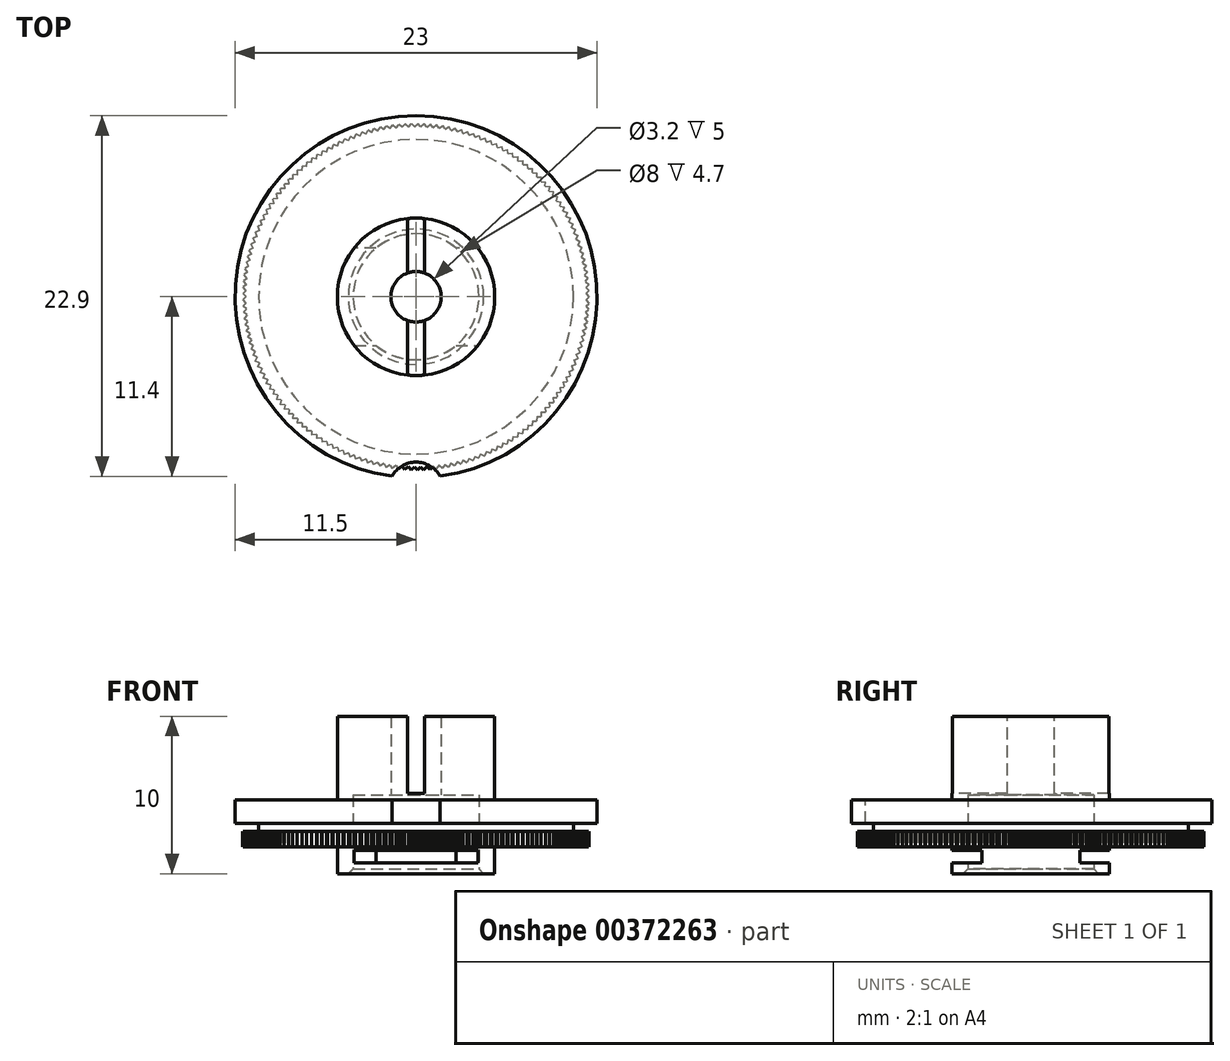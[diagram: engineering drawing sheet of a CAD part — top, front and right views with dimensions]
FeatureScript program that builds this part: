
annotation { "Feature Type Name" : "Feature", "Feature Type Description" : "" }
export const myFeature = defineFeature(function(context is Context, id is Id, definition is map)
    precondition{}
    {
        {
            var Q0;
            Q0=qCreatedBy(makeId("Front.planeOp"),FACE);
            var sketch = newSketch(context, id + "F0", { "sketchPlane" : qUnion([Q0])});
            skLineSegment(sketch, "E0", {"start": v(5, 0) * mm, "end": v(5, 1.7) * mm});
            skLineSegment(sketch, "E1", {"start": v(5, 1.7) * mm, "end": v(11, 1.7) * mm});
            skLineSegment(sketch, "E2", {"start": v(11, 1.7) * mm, "end": v(11, 2.7) * mm});
            skLineSegment(sketch, "E3", {"start": v(11, 2.7) * mm, "end": v(10, 2.7) * mm});
            skLineSegment(sketch, "E4", {"start": v(10, 2.7) * mm, "end": v(10, 3.2) * mm});
            skLineSegment(sketch, "E5", {"start": v(10, 3.2) * mm, "end": v(11.5, 3.2) * mm});
            skLineSegment(sketch, "E6", {"start": v(11.5, 3.2) * mm, "end": v(11.5, 4.7) * mm});
            skLineSegment(sketch, "E7", {"start": v(11.5, 4.7) * mm, "end": v(5, 4.7) * mm});
            skLineSegment(sketch, "E8", {"start": v(5, 4.7) * mm, "end": v(5, 10) * mm});
            skLineSegment(sketch, "E9", {"start": v(5, 10) * mm, "end": v(1.6, 10) * mm});
            skLineSegment(sketch, "E10", {"start": v(1.6, 10) * mm, "end": v(1.6, 5) * mm});
            skLineSegment(sketch, "E11", {"start": v(1.6, 5) * mm, "end": v(4, 5) * mm});
            skLineSegment(sketch, "E12", {"start": v(4, 5) * mm, "end": v(4, 0.3) * mm});
            skLineSegment(sketch, "E13", {"start": v(4, 0.3) * mm, "end": v(4.3, 0) * mm});
            skLineSegment(sketch, "E14", {"start": v(4.3, 0) * mm, "end": v(5, 0) * mm});
            skLineSegment(sketch, "E15", {"start": v(0, 0) * mm, "end": v(0, 10) * mm, "construction": true});
            skSolve(sketch);
        }
        {
            var Q0;
            Q0=makeQuery(id+"F0.imprint","IMPRINT",FACE,{"disambiguationData":[TD([[makeQuery(id+"F0.imprint","IMPRINT",EDGE,{"derivedFrom":sQuery(id+"F0.wireOp",EDGE,"E0")}),1.0]])]});
            var Q1;
            Q1=sQuery(id+"F0.wireOp",EDGE,"E15");
            revolve(context, id + "F1", {"entities" : qUnion([Q0]), "axis" : qUnion([Q1]), "revolveType" : RevolveType.FULL});
        }
        {
            var Q0;
            Q0=makeQuery(id+"F1.opRevolve","SWEPT_FACE",FACE,{"disambiguationData":[OSD([sQuery(id+"F0.wireOp",EDGE,"E1")])]});
            var sketch = newSketch(context, id + "F2", { "sketchPlane" : qUnion([Q0])});
            skCircle(sketch, "E16", {"center": v(0, 0) * mm, "radius": 10.8 * mm});
            skLineSegment(sketch, "E17", {"start": v(-10.8, 0) * mm, "end": v(-11, 0.18) * mm});
            skLineSegment(sketch, "E18", {"start": v(-10.8, 0) * mm, "end": v(-11, -0.22) * mm});
            skLineSegment(sketch, "E19", {"start": v(-10.8, 0) * mm, "end": v(-11, 0) * mm, "construction": true});
            skSolve(sketch);
        }
        {
            var Q0;
            {var subQ2=sQuery(id+"F2.wireOp",EDGE,"E17");Q0=makeQuery(id+"F2.imprint","IMPRINT",FACE,{"disambiguationData":[TD([[makeQuery(id+"F2.imprint","IMPRINT",EDGE,{"derivedFrom":subQ2}),1.0]])]});}
            var Q1;
            Q1=makeQuery(id+"F1.opRevolve","SWEPT_FACE",FACE,{"disambiguationData":[OSD([sQuery(id+"F0.wireOp",EDGE,"E3")])]});
            extrude(context, id + "F3", {"entities" : qUnion([Q0]), "endBound" : BoundingType.UP_TO_SURFACE, "oppositeDirection" : true, "endBoundEntityFace" : qUnion([Q1]), "depth" : 25 * mm});
        }
        {
            var Q0;
            Q0=makeQuery(id+"F3.opExtrude","SWEPT_BODY",BODY,{"disambiguationData":[OSD([sQuery(id+"F0.wireOp",EDGE,"E1"),sQuery(id+"F0.wireOp",EDGE,"E2"),sQuery(id+"F2.wireOp",EDGE,"E17"),sQuery(id+"F2.wireOp",EDGE,"E18")])]});
            var Q1;
            Q1=sQuery(id+"F0.wireOp",EDGE,"E15");
            circularPattern(context, id + "F4", {"entities" : qUnion([Q0]), "axis" : qUnion([Q1]), "angle" : 357.93 * degree, "instanceCount" : round(173), "equalSpace" : true, "computeTransformsWithoutBuiltin" : true});
        }
        {
            var Q0;
            Q0=makeQuery(id+"F4.opPattern","COPY",BODY,{"derivedFrom":makeQuery(id+"F3.opExtrude","SWEPT_BODY",BODY,{"disambiguationData":[OSD([sQuery(id+"F0.wireOp",EDGE,"E1"),sQuery(id+"F0.wireOp",EDGE,"E2"),sQuery(id+"F2.wireOp",EDGE,"E17"),sQuery(id+"F2.wireOp",EDGE,"E18")])]}),"instanceName":"168"});
            var Q1;
            Q1=makeQuery(id+"F4.opPattern","COPY",BODY,{"derivedFrom":makeQuery(id+"F3.opExtrude","SWEPT_BODY",BODY,{"disambiguationData":[OSD([sQuery(id+"F0.wireOp",EDGE,"E1"),sQuery(id+"F0.wireOp",EDGE,"E2"),sQuery(id+"F2.wireOp",EDGE,"E17"),sQuery(id+"F2.wireOp",EDGE,"E18")])]}),"instanceName":"7"});
            var Q2;
            Q2=makeQuery(id+"F4.opPattern","COPY",BODY,{"derivedFrom":makeQuery(id+"F3.opExtrude","SWEPT_BODY",BODY,{"disambiguationData":[OSD([sQuery(id+"F0.wireOp",EDGE,"E1"),sQuery(id+"F0.wireOp",EDGE,"E2"),sQuery(id+"F2.wireOp",EDGE,"E17"),sQuery(id+"F2.wireOp",EDGE,"E18")])]}),"instanceName":"55"});
            var Q3;
            Q3=makeQuery(id+"F4.opPattern","COPY",BODY,{"derivedFrom":makeQuery(id+"F3.opExtrude","SWEPT_BODY",BODY,{"disambiguationData":[OSD([sQuery(id+"F0.wireOp",EDGE,"E1"),sQuery(id+"F0.wireOp",EDGE,"E2"),sQuery(id+"F2.wireOp",EDGE,"E17"),sQuery(id+"F2.wireOp",EDGE,"E18")])]}),"instanceName":"157"});
            var Q4;
            Q4=makeQuery(id+"F4.opPattern","COPY",BODY,{"derivedFrom":makeQuery(id+"F3.opExtrude","SWEPT_BODY",BODY,{"disambiguationData":[OSD([sQuery(id+"F0.wireOp",EDGE,"E1"),sQuery(id+"F0.wireOp",EDGE,"E2"),sQuery(id+"F2.wireOp",EDGE,"E17"),sQuery(id+"F2.wireOp",EDGE,"E18")])]}),"instanceName":"36"});
            var Q5;
            Q5=makeQuery(id+"F4.opPattern","COPY",BODY,{"derivedFrom":makeQuery(id+"F3.opExtrude","SWEPT_BODY",BODY,{"disambiguationData":[OSD([sQuery(id+"F0.wireOp",EDGE,"E1"),sQuery(id+"F0.wireOp",EDGE,"E2"),sQuery(id+"F2.wireOp",EDGE,"E17"),sQuery(id+"F2.wireOp",EDGE,"E18")])]}),"instanceName":"127"});
            var Q6;
            Q6=makeQuery(id+"F4.opPattern","COPY",BODY,{"derivedFrom":makeQuery(id+"F3.opExtrude","SWEPT_BODY",BODY,{"disambiguationData":[OSD([sQuery(id+"F0.wireOp",EDGE,"E1"),sQuery(id+"F0.wireOp",EDGE,"E2"),sQuery(id+"F2.wireOp",EDGE,"E17"),sQuery(id+"F2.wireOp",EDGE,"E18")])]}),"instanceName":"138"});
            var Q7;
            Q7=makeQuery(id+"F4.opPattern","COPY",BODY,{"derivedFrom":makeQuery(id+"F3.opExtrude","SWEPT_BODY",BODY,{"disambiguationData":[OSD([sQuery(id+"F0.wireOp",EDGE,"E1"),sQuery(id+"F0.wireOp",EDGE,"E2"),sQuery(id+"F2.wireOp",EDGE,"E17"),sQuery(id+"F2.wireOp",EDGE,"E18")])]}),"instanceName":"3"});
            var Q8;
            Q8=makeQuery(id+"F4.opPattern","COPY",BODY,{"derivedFrom":makeQuery(id+"F3.opExtrude","SWEPT_BODY",BODY,{"disambiguationData":[OSD([sQuery(id+"F0.wireOp",EDGE,"E1"),sQuery(id+"F0.wireOp",EDGE,"E2"),sQuery(id+"F2.wireOp",EDGE,"E17"),sQuery(id+"F2.wireOp",EDGE,"E18")])]}),"instanceName":"66"});
            var Q9;
            Q9=makeQuery(id+"F4.opPattern","COPY",BODY,{"derivedFrom":makeQuery(id+"F3.opExtrude","SWEPT_BODY",BODY,{"disambiguationData":[OSD([sQuery(id+"F0.wireOp",EDGE,"E1"),sQuery(id+"F0.wireOp",EDGE,"E2"),sQuery(id+"F2.wireOp",EDGE,"E17"),sQuery(id+"F2.wireOp",EDGE,"E18")])]}),"instanceName":"4"});
            var Q10;
            Q10=makeQuery(id+"F4.opPattern","COPY",BODY,{"derivedFrom":makeQuery(id+"F3.opExtrude","SWEPT_BODY",BODY,{"disambiguationData":[OSD([sQuery(id+"F0.wireOp",EDGE,"E1"),sQuery(id+"F0.wireOp",EDGE,"E2"),sQuery(id+"F2.wireOp",EDGE,"E17"),sQuery(id+"F2.wireOp",EDGE,"E18")])]}),"instanceName":"39"});
            var Q11;
            Q11=makeQuery(id+"F4.opPattern","COPY",BODY,{"derivedFrom":makeQuery(id+"F3.opExtrude","SWEPT_BODY",BODY,{"disambiguationData":[OSD([sQuery(id+"F0.wireOp",EDGE,"E1"),sQuery(id+"F0.wireOp",EDGE,"E2"),sQuery(id+"F2.wireOp",EDGE,"E17"),sQuery(id+"F2.wireOp",EDGE,"E18")])]}),"instanceName":"67"});
            var Q12;
            Q12=makeQuery(id+"F4.opPattern","COPY",BODY,{"derivedFrom":makeQuery(id+"F3.opExtrude","SWEPT_BODY",BODY,{"disambiguationData":[OSD([sQuery(id+"F0.wireOp",EDGE,"E1"),sQuery(id+"F0.wireOp",EDGE,"E2"),sQuery(id+"F2.wireOp",EDGE,"E17"),sQuery(id+"F2.wireOp",EDGE,"E18")])]}),"instanceName":"65"});
            var Q13;
            Q13=makeQuery(id+"F4.opPattern","COPY",BODY,{"derivedFrom":makeQuery(id+"F3.opExtrude","SWEPT_BODY",BODY,{"disambiguationData":[OSD([sQuery(id+"F0.wireOp",EDGE,"E1"),sQuery(id+"F0.wireOp",EDGE,"E2"),sQuery(id+"F2.wireOp",EDGE,"E17"),sQuery(id+"F2.wireOp",EDGE,"E18")])]}),"instanceName":"41"});
            var Q14;
            Q14=makeQuery(id+"F4.opPattern","COPY",BODY,{"derivedFrom":makeQuery(id+"F3.opExtrude","SWEPT_BODY",BODY,{"disambiguationData":[OSD([sQuery(id+"F0.wireOp",EDGE,"E1"),sQuery(id+"F0.wireOp",EDGE,"E2"),sQuery(id+"F2.wireOp",EDGE,"E17"),sQuery(id+"F2.wireOp",EDGE,"E18")])]}),"instanceName":"82"});
            var Q15;
            Q15=makeQuery(id+"F4.opPattern","COPY",BODY,{"derivedFrom":makeQuery(id+"F3.opExtrude","SWEPT_BODY",BODY,{"disambiguationData":[OSD([sQuery(id+"F0.wireOp",EDGE,"E1"),sQuery(id+"F0.wireOp",EDGE,"E2"),sQuery(id+"F2.wireOp",EDGE,"E17"),sQuery(id+"F2.wireOp",EDGE,"E18")])]}),"instanceName":"45"});
            var Q16;
            Q16=makeQuery(id+"F4.opPattern","COPY",BODY,{"derivedFrom":makeQuery(id+"F3.opExtrude","SWEPT_BODY",BODY,{"disambiguationData":[OSD([sQuery(id+"F0.wireOp",EDGE,"E1"),sQuery(id+"F0.wireOp",EDGE,"E2"),sQuery(id+"F2.wireOp",EDGE,"E17"),sQuery(id+"F2.wireOp",EDGE,"E18")])]}),"instanceName":"100"});
            var Q17;
            Q17=makeQuery(id+"F4.opPattern","COPY",BODY,{"derivedFrom":makeQuery(id+"F3.opExtrude","SWEPT_BODY",BODY,{"disambiguationData":[OSD([sQuery(id+"F0.wireOp",EDGE,"E1"),sQuery(id+"F0.wireOp",EDGE,"E2"),sQuery(id+"F2.wireOp",EDGE,"E17"),sQuery(id+"F2.wireOp",EDGE,"E18")])]}),"instanceName":"74"});
            var Q18;
            Q18=makeQuery(id+"F4.opPattern","COPY",BODY,{"derivedFrom":makeQuery(id+"F3.opExtrude","SWEPT_BODY",BODY,{"disambiguationData":[OSD([sQuery(id+"F0.wireOp",EDGE,"E1"),sQuery(id+"F0.wireOp",EDGE,"E2"),sQuery(id+"F2.wireOp",EDGE,"E17"),sQuery(id+"F2.wireOp",EDGE,"E18")])]}),"instanceName":"84"});
            var Q19;
            Q19=makeQuery(id+"F4.opPattern","COPY",BODY,{"derivedFrom":makeQuery(id+"F3.opExtrude","SWEPT_BODY",BODY,{"disambiguationData":[OSD([sQuery(id+"F0.wireOp",EDGE,"E1"),sQuery(id+"F0.wireOp",EDGE,"E2"),sQuery(id+"F2.wireOp",EDGE,"E17"),sQuery(id+"F2.wireOp",EDGE,"E18")])]}),"instanceName":"117"});
            var Q20;
            Q20=makeQuery(id+"F4.opPattern","COPY",BODY,{"derivedFrom":makeQuery(id+"F3.opExtrude","SWEPT_BODY",BODY,{"disambiguationData":[OSD([sQuery(id+"F0.wireOp",EDGE,"E1"),sQuery(id+"F0.wireOp",EDGE,"E2"),sQuery(id+"F2.wireOp",EDGE,"E17"),sQuery(id+"F2.wireOp",EDGE,"E18")])]}),"instanceName":"27"});
            var Q21;
            Q21=makeQuery(id+"F4.opPattern","COPY",BODY,{"derivedFrom":makeQuery(id+"F3.opExtrude","SWEPT_BODY",BODY,{"disambiguationData":[OSD([sQuery(id+"F0.wireOp",EDGE,"E1"),sQuery(id+"F0.wireOp",EDGE,"E2"),sQuery(id+"F2.wireOp",EDGE,"E17"),sQuery(id+"F2.wireOp",EDGE,"E18")])]}),"instanceName":"13"});
            var Q22;
            Q22=makeQuery(id+"F4.opPattern","COPY",BODY,{"derivedFrom":makeQuery(id+"F3.opExtrude","SWEPT_BODY",BODY,{"disambiguationData":[OSD([sQuery(id+"F0.wireOp",EDGE,"E1"),sQuery(id+"F0.wireOp",EDGE,"E2"),sQuery(id+"F2.wireOp",EDGE,"E17"),sQuery(id+"F2.wireOp",EDGE,"E18")])]}),"instanceName":"148"});
            var Q23;
            Q23=makeQuery(id+"F4.opPattern","COPY",BODY,{"derivedFrom":makeQuery(id+"F3.opExtrude","SWEPT_BODY",BODY,{"disambiguationData":[OSD([sQuery(id+"F0.wireOp",EDGE,"E1"),sQuery(id+"F0.wireOp",EDGE,"E2"),sQuery(id+"F2.wireOp",EDGE,"E17"),sQuery(id+"F2.wireOp",EDGE,"E18")])]}),"instanceName":"23"});
            var Q24;
            Q24=makeQuery(id+"F4.opPattern","COPY",BODY,{"derivedFrom":makeQuery(id+"F3.opExtrude","SWEPT_BODY",BODY,{"disambiguationData":[OSD([sQuery(id+"F0.wireOp",EDGE,"E1"),sQuery(id+"F0.wireOp",EDGE,"E2"),sQuery(id+"F2.wireOp",EDGE,"E17"),sQuery(id+"F2.wireOp",EDGE,"E18")])]}),"instanceName":"88"});
            var Q25;
            Q25=makeQuery(id+"F4.opPattern","COPY",BODY,{"derivedFrom":makeQuery(id+"F3.opExtrude","SWEPT_BODY",BODY,{"disambiguationData":[OSD([sQuery(id+"F0.wireOp",EDGE,"E1"),sQuery(id+"F0.wireOp",EDGE,"E2"),sQuery(id+"F2.wireOp",EDGE,"E17"),sQuery(id+"F2.wireOp",EDGE,"E18")])]}),"instanceName":"62"});
            var Q26;
            Q26=makeQuery(id+"F4.opPattern","COPY",BODY,{"derivedFrom":makeQuery(id+"F3.opExtrude","SWEPT_BODY",BODY,{"disambiguationData":[OSD([sQuery(id+"F0.wireOp",EDGE,"E1"),sQuery(id+"F0.wireOp",EDGE,"E2"),sQuery(id+"F2.wireOp",EDGE,"E17"),sQuery(id+"F2.wireOp",EDGE,"E18")])]}),"instanceName":"1"});
            var Q27;
            Q27=makeQuery(id+"F4.opPattern","COPY",BODY,{"derivedFrom":makeQuery(id+"F3.opExtrude","SWEPT_BODY",BODY,{"disambiguationData":[OSD([sQuery(id+"F0.wireOp",EDGE,"E1"),sQuery(id+"F0.wireOp",EDGE,"E2"),sQuery(id+"F2.wireOp",EDGE,"E17"),sQuery(id+"F2.wireOp",EDGE,"E18")])]}),"instanceName":"40"});
            var Q28;
            Q28=makeQuery(id+"F4.opPattern","COPY",BODY,{"derivedFrom":makeQuery(id+"F3.opExtrude","SWEPT_BODY",BODY,{"disambiguationData":[OSD([sQuery(id+"F0.wireOp",EDGE,"E1"),sQuery(id+"F0.wireOp",EDGE,"E2"),sQuery(id+"F2.wireOp",EDGE,"E17"),sQuery(id+"F2.wireOp",EDGE,"E18")])]}),"instanceName":"170"});
            var Q29;
            Q29=makeQuery(id+"F4.opPattern","COPY",BODY,{"derivedFrom":makeQuery(id+"F3.opExtrude","SWEPT_BODY",BODY,{"disambiguationData":[OSD([sQuery(id+"F0.wireOp",EDGE,"E1"),sQuery(id+"F0.wireOp",EDGE,"E2"),sQuery(id+"F2.wireOp",EDGE,"E17"),sQuery(id+"F2.wireOp",EDGE,"E18")])]}),"instanceName":"122"});
            var Q30;
            Q30=makeQuery(id+"F4.opPattern","COPY",BODY,{"derivedFrom":makeQuery(id+"F3.opExtrude","SWEPT_BODY",BODY,{"disambiguationData":[OSD([sQuery(id+"F0.wireOp",EDGE,"E1"),sQuery(id+"F0.wireOp",EDGE,"E2"),sQuery(id+"F2.wireOp",EDGE,"E17"),sQuery(id+"F2.wireOp",EDGE,"E18")])]}),"instanceName":"149"});
            var Q31;
            Q31=makeQuery(id+"F4.opPattern","COPY",BODY,{"derivedFrom":makeQuery(id+"F3.opExtrude","SWEPT_BODY",BODY,{"disambiguationData":[OSD([sQuery(id+"F0.wireOp",EDGE,"E1"),sQuery(id+"F0.wireOp",EDGE,"E2"),sQuery(id+"F2.wireOp",EDGE,"E17"),sQuery(id+"F2.wireOp",EDGE,"E18")])]}),"instanceName":"10"});
            var Q32;
            Q32=makeQuery(id+"F4.opPattern","COPY",BODY,{"derivedFrom":makeQuery(id+"F3.opExtrude","SWEPT_BODY",BODY,{"disambiguationData":[OSD([sQuery(id+"F0.wireOp",EDGE,"E1"),sQuery(id+"F0.wireOp",EDGE,"E2"),sQuery(id+"F2.wireOp",EDGE,"E17"),sQuery(id+"F2.wireOp",EDGE,"E18")])]}),"instanceName":"51"});
            var Q33;
            Q33=makeQuery(id+"F4.opPattern","COPY",BODY,{"derivedFrom":makeQuery(id+"F3.opExtrude","SWEPT_BODY",BODY,{"disambiguationData":[OSD([sQuery(id+"F0.wireOp",EDGE,"E1"),sQuery(id+"F0.wireOp",EDGE,"E2"),sQuery(id+"F2.wireOp",EDGE,"E17"),sQuery(id+"F2.wireOp",EDGE,"E18")])]}),"instanceName":"146"});
            var Q34;
            Q34=makeQuery(id+"F4.opPattern","COPY",BODY,{"derivedFrom":makeQuery(id+"F3.opExtrude","SWEPT_BODY",BODY,{"disambiguationData":[OSD([sQuery(id+"F0.wireOp",EDGE,"E1"),sQuery(id+"F0.wireOp",EDGE,"E2"),sQuery(id+"F2.wireOp",EDGE,"E17"),sQuery(id+"F2.wireOp",EDGE,"E18")])]}),"instanceName":"34"});
            var Q35;
            Q35=makeQuery(id+"F4.opPattern","COPY",BODY,{"derivedFrom":makeQuery(id+"F3.opExtrude","SWEPT_BODY",BODY,{"disambiguationData":[OSD([sQuery(id+"F0.wireOp",EDGE,"E1"),sQuery(id+"F0.wireOp",EDGE,"E2"),sQuery(id+"F2.wireOp",EDGE,"E17"),sQuery(id+"F2.wireOp",EDGE,"E18")])]}),"instanceName":"125"});
            var Q36;
            Q36=makeQuery(id+"F4.opPattern","COPY",BODY,{"derivedFrom":makeQuery(id+"F3.opExtrude","SWEPT_BODY",BODY,{"disambiguationData":[OSD([sQuery(id+"F0.wireOp",EDGE,"E1"),sQuery(id+"F0.wireOp",EDGE,"E2"),sQuery(id+"F2.wireOp",EDGE,"E17"),sQuery(id+"F2.wireOp",EDGE,"E18")])]}),"instanceName":"53"});
            var Q37;
            Q37=makeQuery(id+"F4.opPattern","COPY",BODY,{"derivedFrom":makeQuery(id+"F3.opExtrude","SWEPT_BODY",BODY,{"disambiguationData":[OSD([sQuery(id+"F0.wireOp",EDGE,"E1"),sQuery(id+"F0.wireOp",EDGE,"E2"),sQuery(id+"F2.wireOp",EDGE,"E17"),sQuery(id+"F2.wireOp",EDGE,"E18")])]}),"instanceName":"165"});
            var Q38;
            Q38=makeQuery(id+"F4.opPattern","COPY",BODY,{"derivedFrom":makeQuery(id+"F3.opExtrude","SWEPT_BODY",BODY,{"disambiguationData":[OSD([sQuery(id+"F0.wireOp",EDGE,"E1"),sQuery(id+"F0.wireOp",EDGE,"E2"),sQuery(id+"F2.wireOp",EDGE,"E17"),sQuery(id+"F2.wireOp",EDGE,"E18")])]}),"instanceName":"98"});
            var Q39;
            Q39=makeQuery(id+"F4.opPattern","COPY",BODY,{"derivedFrom":makeQuery(id+"F3.opExtrude","SWEPT_BODY",BODY,{"disambiguationData":[OSD([sQuery(id+"F0.wireOp",EDGE,"E1"),sQuery(id+"F0.wireOp",EDGE,"E2"),sQuery(id+"F2.wireOp",EDGE,"E17"),sQuery(id+"F2.wireOp",EDGE,"E18")])]}),"instanceName":"128"});
            var Q40;
            Q40=makeQuery(id+"F4.opPattern","COPY",BODY,{"derivedFrom":makeQuery(id+"F3.opExtrude","SWEPT_BODY",BODY,{"disambiguationData":[OSD([sQuery(id+"F0.wireOp",EDGE,"E1"),sQuery(id+"F0.wireOp",EDGE,"E2"),sQuery(id+"F2.wireOp",EDGE,"E17"),sQuery(id+"F2.wireOp",EDGE,"E18")])]}),"instanceName":"130"});
            var Q41;
            Q41=makeQuery(id+"F4.opPattern","COPY",BODY,{"derivedFrom":makeQuery(id+"F3.opExtrude","SWEPT_BODY",BODY,{"disambiguationData":[OSD([sQuery(id+"F0.wireOp",EDGE,"E1"),sQuery(id+"F0.wireOp",EDGE,"E2"),sQuery(id+"F2.wireOp",EDGE,"E17"),sQuery(id+"F2.wireOp",EDGE,"E18")])]}),"instanceName":"24"});
            var Q42;
            Q42=makeQuery(id+"F4.opPattern","COPY",BODY,{"derivedFrom":makeQuery(id+"F3.opExtrude","SWEPT_BODY",BODY,{"disambiguationData":[OSD([sQuery(id+"F0.wireOp",EDGE,"E1"),sQuery(id+"F0.wireOp",EDGE,"E2"),sQuery(id+"F2.wireOp",EDGE,"E17"),sQuery(id+"F2.wireOp",EDGE,"E18")])]}),"instanceName":"52"});
            var Q43;
            Q43=makeQuery(id+"F4.opPattern","COPY",BODY,{"derivedFrom":makeQuery(id+"F3.opExtrude","SWEPT_BODY",BODY,{"disambiguationData":[OSD([sQuery(id+"F0.wireOp",EDGE,"E1"),sQuery(id+"F0.wireOp",EDGE,"E2"),sQuery(id+"F2.wireOp",EDGE,"E17"),sQuery(id+"F2.wireOp",EDGE,"E18")])]}),"instanceName":"156"});
            var Q44;
            Q44=makeQuery(id+"F4.opPattern","COPY",BODY,{"derivedFrom":makeQuery(id+"F3.opExtrude","SWEPT_BODY",BODY,{"disambiguationData":[OSD([sQuery(id+"F0.wireOp",EDGE,"E1"),sQuery(id+"F0.wireOp",EDGE,"E2"),sQuery(id+"F2.wireOp",EDGE,"E17"),sQuery(id+"F2.wireOp",EDGE,"E18")])]}),"instanceName":"77"});
            var Q45;
            Q45=makeQuery(id+"F4.opPattern","COPY",BODY,{"derivedFrom":makeQuery(id+"F3.opExtrude","SWEPT_BODY",BODY,{"disambiguationData":[OSD([sQuery(id+"F0.wireOp",EDGE,"E1"),sQuery(id+"F0.wireOp",EDGE,"E2"),sQuery(id+"F2.wireOp",EDGE,"E17"),sQuery(id+"F2.wireOp",EDGE,"E18")])]}),"instanceName":"108"});
            var Q46;
            Q46=makeQuery(id+"F4.opPattern","COPY",BODY,{"derivedFrom":makeQuery(id+"F3.opExtrude","SWEPT_BODY",BODY,{"disambiguationData":[OSD([sQuery(id+"F0.wireOp",EDGE,"E1"),sQuery(id+"F0.wireOp",EDGE,"E2"),sQuery(id+"F2.wireOp",EDGE,"E17"),sQuery(id+"F2.wireOp",EDGE,"E18")])]}),"instanceName":"169"});
            var Q47;
            Q47=makeQuery(id+"F4.opPattern","COPY",BODY,{"derivedFrom":makeQuery(id+"F3.opExtrude","SWEPT_BODY",BODY,{"disambiguationData":[OSD([sQuery(id+"F0.wireOp",EDGE,"E1"),sQuery(id+"F0.wireOp",EDGE,"E2"),sQuery(id+"F2.wireOp",EDGE,"E17"),sQuery(id+"F2.wireOp",EDGE,"E18")])]}),"instanceName":"64"});
            var Q48;
            Q48=makeQuery(id+"F3.opExtrude","SWEPT_BODY",BODY,{"disambiguationData":[OSD([sQuery(id+"F0.wireOp",EDGE,"E1"),sQuery(id+"F0.wireOp",EDGE,"E2"),sQuery(id+"F2.wireOp",EDGE,"E17"),sQuery(id+"F2.wireOp",EDGE,"E18")])]});
            var Q49;
            Q49=makeQuery(id+"F4.opPattern","COPY",BODY,{"derivedFrom":makeQuery(id+"F3.opExtrude","SWEPT_BODY",BODY,{"disambiguationData":[OSD([sQuery(id+"F0.wireOp",EDGE,"E1"),sQuery(id+"F0.wireOp",EDGE,"E2"),sQuery(id+"F2.wireOp",EDGE,"E17"),sQuery(id+"F2.wireOp",EDGE,"E18")])]}),"instanceName":"126"});
            var Q50;
            Q50=makeQuery(id+"F4.opPattern","COPY",BODY,{"derivedFrom":makeQuery(id+"F3.opExtrude","SWEPT_BODY",BODY,{"disambiguationData":[OSD([sQuery(id+"F0.wireOp",EDGE,"E1"),sQuery(id+"F0.wireOp",EDGE,"E2"),sQuery(id+"F2.wireOp",EDGE,"E17"),sQuery(id+"F2.wireOp",EDGE,"E18")])]}),"instanceName":"140"});
            var Q51;
            Q51=makeQuery(id+"F4.opPattern","COPY",BODY,{"derivedFrom":makeQuery(id+"F3.opExtrude","SWEPT_BODY",BODY,{"disambiguationData":[OSD([sQuery(id+"F0.wireOp",EDGE,"E1"),sQuery(id+"F0.wireOp",EDGE,"E2"),sQuery(id+"F2.wireOp",EDGE,"E17"),sQuery(id+"F2.wireOp",EDGE,"E18")])]}),"instanceName":"14"});
            var Q52;
            Q52=makeQuery(id+"F4.opPattern","COPY",BODY,{"derivedFrom":makeQuery(id+"F3.opExtrude","SWEPT_BODY",BODY,{"disambiguationData":[OSD([sQuery(id+"F0.wireOp",EDGE,"E1"),sQuery(id+"F0.wireOp",EDGE,"E2"),sQuery(id+"F2.wireOp",EDGE,"E17"),sQuery(id+"F2.wireOp",EDGE,"E18")])]}),"instanceName":"78"});
            var Q53;
            Q53=makeQuery(id+"F4.opPattern","COPY",BODY,{"derivedFrom":makeQuery(id+"F3.opExtrude","SWEPT_BODY",BODY,{"disambiguationData":[OSD([sQuery(id+"F0.wireOp",EDGE,"E1"),sQuery(id+"F0.wireOp",EDGE,"E2"),sQuery(id+"F2.wireOp",EDGE,"E17"),sQuery(id+"F2.wireOp",EDGE,"E18")])]}),"instanceName":"147"});
            var Q54;
            Q54=makeQuery(id+"F4.opPattern","COPY",BODY,{"derivedFrom":makeQuery(id+"F3.opExtrude","SWEPT_BODY",BODY,{"disambiguationData":[OSD([sQuery(id+"F0.wireOp",EDGE,"E1"),sQuery(id+"F0.wireOp",EDGE,"E2"),sQuery(id+"F2.wireOp",EDGE,"E17"),sQuery(id+"F2.wireOp",EDGE,"E18")])]}),"instanceName":"154"});
            var Q55;
            Q55=makeQuery(id+"F4.opPattern","COPY",BODY,{"derivedFrom":makeQuery(id+"F3.opExtrude","SWEPT_BODY",BODY,{"disambiguationData":[OSD([sQuery(id+"F0.wireOp",EDGE,"E1"),sQuery(id+"F0.wireOp",EDGE,"E2"),sQuery(id+"F2.wireOp",EDGE,"E17"),sQuery(id+"F2.wireOp",EDGE,"E18")])]}),"instanceName":"15"});
            var Q56;
            Q56=makeQuery(id+"F4.opPattern","COPY",BODY,{"derivedFrom":makeQuery(id+"F3.opExtrude","SWEPT_BODY",BODY,{"disambiguationData":[OSD([sQuery(id+"F0.wireOp",EDGE,"E1"),sQuery(id+"F0.wireOp",EDGE,"E2"),sQuery(id+"F2.wireOp",EDGE,"E17"),sQuery(id+"F2.wireOp",EDGE,"E18")])]}),"instanceName":"116"});
            var Q57;
            Q57=makeQuery(id+"F4.opPattern","COPY",BODY,{"derivedFrom":makeQuery(id+"F3.opExtrude","SWEPT_BODY",BODY,{"disambiguationData":[OSD([sQuery(id+"F0.wireOp",EDGE,"E1"),sQuery(id+"F0.wireOp",EDGE,"E2"),sQuery(id+"F2.wireOp",EDGE,"E17"),sQuery(id+"F2.wireOp",EDGE,"E18")])]}),"instanceName":"110"});
            var Q58;
            Q58=makeQuery(id+"F4.opPattern","COPY",BODY,{"derivedFrom":makeQuery(id+"F3.opExtrude","SWEPT_BODY",BODY,{"disambiguationData":[OSD([sQuery(id+"F0.wireOp",EDGE,"E1"),sQuery(id+"F0.wireOp",EDGE,"E2"),sQuery(id+"F2.wireOp",EDGE,"E17"),sQuery(id+"F2.wireOp",EDGE,"E18")])]}),"instanceName":"121"});
            var Q59;
            Q59=makeQuery(id+"F4.opPattern","COPY",BODY,{"derivedFrom":makeQuery(id+"F3.opExtrude","SWEPT_BODY",BODY,{"disambiguationData":[OSD([sQuery(id+"F0.wireOp",EDGE,"E1"),sQuery(id+"F0.wireOp",EDGE,"E2"),sQuery(id+"F2.wireOp",EDGE,"E17"),sQuery(id+"F2.wireOp",EDGE,"E18")])]}),"instanceName":"137"});
            var Q60;
            Q60=makeQuery(id+"F4.opPattern","COPY",BODY,{"derivedFrom":makeQuery(id+"F3.opExtrude","SWEPT_BODY",BODY,{"disambiguationData":[OSD([sQuery(id+"F0.wireOp",EDGE,"E1"),sQuery(id+"F0.wireOp",EDGE,"E2"),sQuery(id+"F2.wireOp",EDGE,"E17"),sQuery(id+"F2.wireOp",EDGE,"E18")])]}),"instanceName":"134"});
            var Q61;
            Q61=makeQuery(id+"F4.opPattern","COPY",BODY,{"derivedFrom":makeQuery(id+"F3.opExtrude","SWEPT_BODY",BODY,{"disambiguationData":[OSD([sQuery(id+"F0.wireOp",EDGE,"E1"),sQuery(id+"F0.wireOp",EDGE,"E2"),sQuery(id+"F2.wireOp",EDGE,"E17"),sQuery(id+"F2.wireOp",EDGE,"E18")])]}),"instanceName":"61"});
            var Q62;
            Q62=makeQuery(id+"F4.opPattern","COPY",BODY,{"derivedFrom":makeQuery(id+"F3.opExtrude","SWEPT_BODY",BODY,{"disambiguationData":[OSD([sQuery(id+"F0.wireOp",EDGE,"E1"),sQuery(id+"F0.wireOp",EDGE,"E2"),sQuery(id+"F2.wireOp",EDGE,"E17"),sQuery(id+"F2.wireOp",EDGE,"E18")])]}),"instanceName":"95"});
            var Q63;
            Q63=makeQuery(id+"F4.opPattern","COPY",BODY,{"derivedFrom":makeQuery(id+"F3.opExtrude","SWEPT_BODY",BODY,{"disambiguationData":[OSD([sQuery(id+"F0.wireOp",EDGE,"E1"),sQuery(id+"F0.wireOp",EDGE,"E2"),sQuery(id+"F2.wireOp",EDGE,"E17"),sQuery(id+"F2.wireOp",EDGE,"E18")])]}),"instanceName":"171"});
            var Q64;
            Q64=makeQuery(id+"F4.opPattern","COPY",BODY,{"derivedFrom":makeQuery(id+"F3.opExtrude","SWEPT_BODY",BODY,{"disambiguationData":[OSD([sQuery(id+"F0.wireOp",EDGE,"E1"),sQuery(id+"F0.wireOp",EDGE,"E2"),sQuery(id+"F2.wireOp",EDGE,"E17"),sQuery(id+"F2.wireOp",EDGE,"E18")])]}),"instanceName":"21"});
            var Q65;
            Q65=makeQuery(id+"F4.opPattern","COPY",BODY,{"derivedFrom":makeQuery(id+"F3.opExtrude","SWEPT_BODY",BODY,{"disambiguationData":[OSD([sQuery(id+"F0.wireOp",EDGE,"E1"),sQuery(id+"F0.wireOp",EDGE,"E2"),sQuery(id+"F2.wireOp",EDGE,"E17"),sQuery(id+"F2.wireOp",EDGE,"E18")])]}),"instanceName":"102"});
            var Q66;
            Q66=makeQuery(id+"F4.opPattern","COPY",BODY,{"derivedFrom":makeQuery(id+"F3.opExtrude","SWEPT_BODY",BODY,{"disambiguationData":[OSD([sQuery(id+"F0.wireOp",EDGE,"E1"),sQuery(id+"F0.wireOp",EDGE,"E2"),sQuery(id+"F2.wireOp",EDGE,"E17"),sQuery(id+"F2.wireOp",EDGE,"E18")])]}),"instanceName":"93"});
            var Q67;
            Q67=makeQuery(id+"F4.opPattern","COPY",BODY,{"derivedFrom":makeQuery(id+"F3.opExtrude","SWEPT_BODY",BODY,{"disambiguationData":[OSD([sQuery(id+"F0.wireOp",EDGE,"E1"),sQuery(id+"F0.wireOp",EDGE,"E2"),sQuery(id+"F2.wireOp",EDGE,"E17"),sQuery(id+"F2.wireOp",EDGE,"E18")])]}),"instanceName":"33"});
            var Q68;
            Q68=makeQuery(id+"F4.opPattern","COPY",BODY,{"derivedFrom":makeQuery(id+"F3.opExtrude","SWEPT_BODY",BODY,{"disambiguationData":[OSD([sQuery(id+"F0.wireOp",EDGE,"E1"),sQuery(id+"F0.wireOp",EDGE,"E2"),sQuery(id+"F2.wireOp",EDGE,"E17"),sQuery(id+"F2.wireOp",EDGE,"E18")])]}),"instanceName":"160"});
            var Q69;
            Q69=makeQuery(id+"F4.opPattern","COPY",BODY,{"derivedFrom":makeQuery(id+"F3.opExtrude","SWEPT_BODY",BODY,{"disambiguationData":[OSD([sQuery(id+"F0.wireOp",EDGE,"E1"),sQuery(id+"F0.wireOp",EDGE,"E2"),sQuery(id+"F2.wireOp",EDGE,"E17"),sQuery(id+"F2.wireOp",EDGE,"E18")])]}),"instanceName":"28"});
            var Q70;
            Q70=makeQuery(id+"F4.opPattern","COPY",BODY,{"derivedFrom":makeQuery(id+"F3.opExtrude","SWEPT_BODY",BODY,{"disambiguationData":[OSD([sQuery(id+"F0.wireOp",EDGE,"E1"),sQuery(id+"F0.wireOp",EDGE,"E2"),sQuery(id+"F2.wireOp",EDGE,"E17"),sQuery(id+"F2.wireOp",EDGE,"E18")])]}),"instanceName":"101"});
            var Q71;
            Q71=makeQuery(id+"F4.opPattern","COPY",BODY,{"derivedFrom":makeQuery(id+"F3.opExtrude","SWEPT_BODY",BODY,{"disambiguationData":[OSD([sQuery(id+"F0.wireOp",EDGE,"E1"),sQuery(id+"F0.wireOp",EDGE,"E2"),sQuery(id+"F2.wireOp",EDGE,"E17"),sQuery(id+"F2.wireOp",EDGE,"E18")])]}),"instanceName":"114"});
            var Q72;
            Q72=makeQuery(id+"F4.opPattern","COPY",BODY,{"derivedFrom":makeQuery(id+"F3.opExtrude","SWEPT_BODY",BODY,{"disambiguationData":[OSD([sQuery(id+"F0.wireOp",EDGE,"E1"),sQuery(id+"F0.wireOp",EDGE,"E2"),sQuery(id+"F2.wireOp",EDGE,"E17"),sQuery(id+"F2.wireOp",EDGE,"E18")])]}),"instanceName":"44"});
            var Q73;
            Q73=makeQuery(id+"F4.opPattern","COPY",BODY,{"derivedFrom":makeQuery(id+"F3.opExtrude","SWEPT_BODY",BODY,{"disambiguationData":[OSD([sQuery(id+"F0.wireOp",EDGE,"E1"),sQuery(id+"F0.wireOp",EDGE,"E2"),sQuery(id+"F2.wireOp",EDGE,"E17"),sQuery(id+"F2.wireOp",EDGE,"E18")])]}),"instanceName":"104"});
            var Q74;
            Q74=makeQuery(id+"F4.opPattern","COPY",BODY,{"derivedFrom":makeQuery(id+"F3.opExtrude","SWEPT_BODY",BODY,{"disambiguationData":[OSD([sQuery(id+"F0.wireOp",EDGE,"E1"),sQuery(id+"F0.wireOp",EDGE,"E2"),sQuery(id+"F2.wireOp",EDGE,"E17"),sQuery(id+"F2.wireOp",EDGE,"E18")])]}),"instanceName":"83"});
            var Q75;
            Q75=makeQuery(id+"F4.opPattern","COPY",BODY,{"derivedFrom":makeQuery(id+"F3.opExtrude","SWEPT_BODY",BODY,{"disambiguationData":[OSD([sQuery(id+"F0.wireOp",EDGE,"E1"),sQuery(id+"F0.wireOp",EDGE,"E2"),sQuery(id+"F2.wireOp",EDGE,"E17"),sQuery(id+"F2.wireOp",EDGE,"E18")])]}),"instanceName":"109"});
            var Q76;
            Q76=makeQuery(id+"F4.opPattern","COPY",BODY,{"derivedFrom":makeQuery(id+"F3.opExtrude","SWEPT_BODY",BODY,{"disambiguationData":[OSD([sQuery(id+"F0.wireOp",EDGE,"E1"),sQuery(id+"F0.wireOp",EDGE,"E2"),sQuery(id+"F2.wireOp",EDGE,"E17"),sQuery(id+"F2.wireOp",EDGE,"E18")])]}),"instanceName":"141"});
            var Q77;
            Q77=makeQuery(id+"F4.opPattern","COPY",BODY,{"derivedFrom":makeQuery(id+"F3.opExtrude","SWEPT_BODY",BODY,{"disambiguationData":[OSD([sQuery(id+"F0.wireOp",EDGE,"E1"),sQuery(id+"F0.wireOp",EDGE,"E2"),sQuery(id+"F2.wireOp",EDGE,"E17"),sQuery(id+"F2.wireOp",EDGE,"E18")])]}),"instanceName":"81"});
            var Q78;
            Q78=makeQuery(id+"F4.opPattern","COPY",BODY,{"derivedFrom":makeQuery(id+"F3.opExtrude","SWEPT_BODY",BODY,{"disambiguationData":[OSD([sQuery(id+"F0.wireOp",EDGE,"E1"),sQuery(id+"F0.wireOp",EDGE,"E2"),sQuery(id+"F2.wireOp",EDGE,"E17"),sQuery(id+"F2.wireOp",EDGE,"E18")])]}),"instanceName":"75"});
            var Q79;
            Q79=makeQuery(id+"F4.opPattern","COPY",BODY,{"derivedFrom":makeQuery(id+"F3.opExtrude","SWEPT_BODY",BODY,{"disambiguationData":[OSD([sQuery(id+"F0.wireOp",EDGE,"E1"),sQuery(id+"F0.wireOp",EDGE,"E2"),sQuery(id+"F2.wireOp",EDGE,"E17"),sQuery(id+"F2.wireOp",EDGE,"E18")])]}),"instanceName":"92"});
            var Q80;
            Q80=makeQuery(id+"F4.opPattern","COPY",BODY,{"derivedFrom":makeQuery(id+"F3.opExtrude","SWEPT_BODY",BODY,{"disambiguationData":[OSD([sQuery(id+"F0.wireOp",EDGE,"E1"),sQuery(id+"F0.wireOp",EDGE,"E2"),sQuery(id+"F2.wireOp",EDGE,"E17"),sQuery(id+"F2.wireOp",EDGE,"E18")])]}),"instanceName":"9"});
            var Q81;
            Q81=makeQuery(id+"F4.opPattern","COPY",BODY,{"derivedFrom":makeQuery(id+"F3.opExtrude","SWEPT_BODY",BODY,{"disambiguationData":[OSD([sQuery(id+"F0.wireOp",EDGE,"E1"),sQuery(id+"F0.wireOp",EDGE,"E2"),sQuery(id+"F2.wireOp",EDGE,"E17"),sQuery(id+"F2.wireOp",EDGE,"E18")])]}),"instanceName":"153"});
            var Q82;
            Q82=makeQuery(id+"F4.opPattern","COPY",BODY,{"derivedFrom":makeQuery(id+"F3.opExtrude","SWEPT_BODY",BODY,{"disambiguationData":[OSD([sQuery(id+"F0.wireOp",EDGE,"E1"),sQuery(id+"F0.wireOp",EDGE,"E2"),sQuery(id+"F2.wireOp",EDGE,"E17"),sQuery(id+"F2.wireOp",EDGE,"E18")])]}),"instanceName":"159"});
            var Q83;
            Q83=makeQuery(id+"F4.opPattern","COPY",BODY,{"derivedFrom":makeQuery(id+"F3.opExtrude","SWEPT_BODY",BODY,{"disambiguationData":[OSD([sQuery(id+"F0.wireOp",EDGE,"E1"),sQuery(id+"F0.wireOp",EDGE,"E2"),sQuery(id+"F2.wireOp",EDGE,"E17"),sQuery(id+"F2.wireOp",EDGE,"E18")])]}),"instanceName":"48"});
            var Q84;
            Q84=makeQuery(id+"F4.opPattern","COPY",BODY,{"derivedFrom":makeQuery(id+"F3.opExtrude","SWEPT_BODY",BODY,{"disambiguationData":[OSD([sQuery(id+"F0.wireOp",EDGE,"E1"),sQuery(id+"F0.wireOp",EDGE,"E2"),sQuery(id+"F2.wireOp",EDGE,"E17"),sQuery(id+"F2.wireOp",EDGE,"E18")])]}),"instanceName":"115"});
            var Q85;
            Q85=makeQuery(id+"F4.opPattern","COPY",BODY,{"derivedFrom":makeQuery(id+"F3.opExtrude","SWEPT_BODY",BODY,{"disambiguationData":[OSD([sQuery(id+"F0.wireOp",EDGE,"E1"),sQuery(id+"F0.wireOp",EDGE,"E2"),sQuery(id+"F2.wireOp",EDGE,"E17"),sQuery(id+"F2.wireOp",EDGE,"E18")])]}),"instanceName":"57"});
            var Q86;
            Q86=makeQuery(id+"F4.opPattern","COPY",BODY,{"derivedFrom":makeQuery(id+"F3.opExtrude","SWEPT_BODY",BODY,{"disambiguationData":[OSD([sQuery(id+"F0.wireOp",EDGE,"E1"),sQuery(id+"F0.wireOp",EDGE,"E2"),sQuery(id+"F2.wireOp",EDGE,"E17"),sQuery(id+"F2.wireOp",EDGE,"E18")])]}),"instanceName":"29"});
            var Q87;
            Q87=makeQuery(id+"F4.opPattern","COPY",BODY,{"derivedFrom":makeQuery(id+"F3.opExtrude","SWEPT_BODY",BODY,{"disambiguationData":[OSD([sQuery(id+"F0.wireOp",EDGE,"E1"),sQuery(id+"F0.wireOp",EDGE,"E2"),sQuery(id+"F2.wireOp",EDGE,"E17"),sQuery(id+"F2.wireOp",EDGE,"E18")])]}),"instanceName":"20"});
            var Q88;
            Q88=makeQuery(id+"F4.opPattern","COPY",BODY,{"derivedFrom":makeQuery(id+"F3.opExtrude","SWEPT_BODY",BODY,{"disambiguationData":[OSD([sQuery(id+"F0.wireOp",EDGE,"E1"),sQuery(id+"F0.wireOp",EDGE,"E2"),sQuery(id+"F2.wireOp",EDGE,"E17"),sQuery(id+"F2.wireOp",EDGE,"E18")])]}),"instanceName":"142"});
            var Q89;
            Q89=makeQuery(id+"F4.opPattern","COPY",BODY,{"derivedFrom":makeQuery(id+"F3.opExtrude","SWEPT_BODY",BODY,{"disambiguationData":[OSD([sQuery(id+"F0.wireOp",EDGE,"E1"),sQuery(id+"F0.wireOp",EDGE,"E2"),sQuery(id+"F2.wireOp",EDGE,"E17"),sQuery(id+"F2.wireOp",EDGE,"E18")])]}),"instanceName":"152"});
            var Q90;
            Q90=makeQuery(id+"F4.opPattern","COPY",BODY,{"derivedFrom":makeQuery(id+"F3.opExtrude","SWEPT_BODY",BODY,{"disambiguationData":[OSD([sQuery(id+"F0.wireOp",EDGE,"E1"),sQuery(id+"F0.wireOp",EDGE,"E2"),sQuery(id+"F2.wireOp",EDGE,"E17"),sQuery(id+"F2.wireOp",EDGE,"E18")])]}),"instanceName":"124"});
            var Q91;
            Q91=makeQuery(id+"F4.opPattern","COPY",BODY,{"derivedFrom":makeQuery(id+"F3.opExtrude","SWEPT_BODY",BODY,{"disambiguationData":[OSD([sQuery(id+"F0.wireOp",EDGE,"E1"),sQuery(id+"F0.wireOp",EDGE,"E2"),sQuery(id+"F2.wireOp",EDGE,"E17"),sQuery(id+"F2.wireOp",EDGE,"E18")])]}),"instanceName":"107"});
            var Q92;
            Q92=makeQuery(id+"F4.opPattern","COPY",BODY,{"derivedFrom":makeQuery(id+"F3.opExtrude","SWEPT_BODY",BODY,{"disambiguationData":[OSD([sQuery(id+"F0.wireOp",EDGE,"E1"),sQuery(id+"F0.wireOp",EDGE,"E2"),sQuery(id+"F2.wireOp",EDGE,"E17"),sQuery(id+"F2.wireOp",EDGE,"E18")])]}),"instanceName":"50"});
            var Q93;
            Q93=makeQuery(id+"F4.opPattern","COPY",BODY,{"derivedFrom":makeQuery(id+"F3.opExtrude","SWEPT_BODY",BODY,{"disambiguationData":[OSD([sQuery(id+"F0.wireOp",EDGE,"E1"),sQuery(id+"F0.wireOp",EDGE,"E2"),sQuery(id+"F2.wireOp",EDGE,"E17"),sQuery(id+"F2.wireOp",EDGE,"E18")])]}),"instanceName":"43"});
            var Q94;
            Q94=makeQuery(id+"F4.opPattern","COPY",BODY,{"derivedFrom":makeQuery(id+"F3.opExtrude","SWEPT_BODY",BODY,{"disambiguationData":[OSD([sQuery(id+"F0.wireOp",EDGE,"E1"),sQuery(id+"F0.wireOp",EDGE,"E2"),sQuery(id+"F2.wireOp",EDGE,"E17"),sQuery(id+"F2.wireOp",EDGE,"E18")])]}),"instanceName":"22"});
            var Q95;
            Q95=makeQuery(id+"F4.opPattern","COPY",BODY,{"derivedFrom":makeQuery(id+"F3.opExtrude","SWEPT_BODY",BODY,{"disambiguationData":[OSD([sQuery(id+"F0.wireOp",EDGE,"E1"),sQuery(id+"F0.wireOp",EDGE,"E2"),sQuery(id+"F2.wireOp",EDGE,"E17"),sQuery(id+"F2.wireOp",EDGE,"E18")])]}),"instanceName":"18"});
            var Q96;
            Q96=makeQuery(id+"F4.opPattern","COPY",BODY,{"derivedFrom":makeQuery(id+"F3.opExtrude","SWEPT_BODY",BODY,{"disambiguationData":[OSD([sQuery(id+"F0.wireOp",EDGE,"E1"),sQuery(id+"F0.wireOp",EDGE,"E2"),sQuery(id+"F2.wireOp",EDGE,"E17"),sQuery(id+"F2.wireOp",EDGE,"E18")])]}),"instanceName":"164"});
            var Q97;
            Q97=makeQuery(id+"F4.opPattern","COPY",BODY,{"derivedFrom":makeQuery(id+"F3.opExtrude","SWEPT_BODY",BODY,{"disambiguationData":[OSD([sQuery(id+"F0.wireOp",EDGE,"E1"),sQuery(id+"F0.wireOp",EDGE,"E2"),sQuery(id+"F2.wireOp",EDGE,"E17"),sQuery(id+"F2.wireOp",EDGE,"E18")])]}),"instanceName":"106"});
            var Q98;
            Q98=makeQuery(id+"F4.opPattern","COPY",BODY,{"derivedFrom":makeQuery(id+"F3.opExtrude","SWEPT_BODY",BODY,{"disambiguationData":[OSD([sQuery(id+"F0.wireOp",EDGE,"E1"),sQuery(id+"F0.wireOp",EDGE,"E2"),sQuery(id+"F2.wireOp",EDGE,"E17"),sQuery(id+"F2.wireOp",EDGE,"E18")])]}),"instanceName":"145"});
            var Q99;
            Q99=makeQuery(id+"F4.opPattern","COPY",BODY,{"derivedFrom":makeQuery(id+"F3.opExtrude","SWEPT_BODY",BODY,{"disambiguationData":[OSD([sQuery(id+"F0.wireOp",EDGE,"E1"),sQuery(id+"F0.wireOp",EDGE,"E2"),sQuery(id+"F2.wireOp",EDGE,"E17"),sQuery(id+"F2.wireOp",EDGE,"E18")])]}),"instanceName":"96"});
            var Q100;
            Q100=makeQuery(id+"F4.opPattern","COPY",BODY,{"derivedFrom":makeQuery(id+"F3.opExtrude","SWEPT_BODY",BODY,{"disambiguationData":[OSD([sQuery(id+"F0.wireOp",EDGE,"E1"),sQuery(id+"F0.wireOp",EDGE,"E2"),sQuery(id+"F2.wireOp",EDGE,"E17"),sQuery(id+"F2.wireOp",EDGE,"E18")])]}),"instanceName":"31"});
            var Q101;
            Q101=makeQuery(id+"F4.opPattern","COPY",BODY,{"derivedFrom":makeQuery(id+"F3.opExtrude","SWEPT_BODY",BODY,{"disambiguationData":[OSD([sQuery(id+"F0.wireOp",EDGE,"E1"),sQuery(id+"F0.wireOp",EDGE,"E2"),sQuery(id+"F2.wireOp",EDGE,"E17"),sQuery(id+"F2.wireOp",EDGE,"E18")])]}),"instanceName":"113"});
            var Q102;
            Q102=makeQuery(id+"F4.opPattern","COPY",BODY,{"derivedFrom":makeQuery(id+"F3.opExtrude","SWEPT_BODY",BODY,{"disambiguationData":[OSD([sQuery(id+"F0.wireOp",EDGE,"E1"),sQuery(id+"F0.wireOp",EDGE,"E2"),sQuery(id+"F2.wireOp",EDGE,"E17"),sQuery(id+"F2.wireOp",EDGE,"E18")])]}),"instanceName":"47"});
            var Q103;
            Q103=makeQuery(id+"F4.opPattern","COPY",BODY,{"derivedFrom":makeQuery(id+"F3.opExtrude","SWEPT_BODY",BODY,{"disambiguationData":[OSD([sQuery(id+"F0.wireOp",EDGE,"E1"),sQuery(id+"F0.wireOp",EDGE,"E2"),sQuery(id+"F2.wireOp",EDGE,"E17"),sQuery(id+"F2.wireOp",EDGE,"E18")])]}),"instanceName":"119"});
            var Q104;
            Q104=makeQuery(id+"F4.opPattern","COPY",BODY,{"derivedFrom":makeQuery(id+"F3.opExtrude","SWEPT_BODY",BODY,{"disambiguationData":[OSD([sQuery(id+"F0.wireOp",EDGE,"E1"),sQuery(id+"F0.wireOp",EDGE,"E2"),sQuery(id+"F2.wireOp",EDGE,"E17"),sQuery(id+"F2.wireOp",EDGE,"E18")])]}),"instanceName":"103"});
            var Q105;
            Q105=makeQuery(id+"F4.opPattern","COPY",BODY,{"derivedFrom":makeQuery(id+"F3.opExtrude","SWEPT_BODY",BODY,{"disambiguationData":[OSD([sQuery(id+"F0.wireOp",EDGE,"E1"),sQuery(id+"F0.wireOp",EDGE,"E2"),sQuery(id+"F2.wireOp",EDGE,"E17"),sQuery(id+"F2.wireOp",EDGE,"E18")])]}),"instanceName":"37"});
            var Q106;
            Q106=makeQuery(id+"F4.opPattern","COPY",BODY,{"derivedFrom":makeQuery(id+"F3.opExtrude","SWEPT_BODY",BODY,{"disambiguationData":[OSD([sQuery(id+"F0.wireOp",EDGE,"E1"),sQuery(id+"F0.wireOp",EDGE,"E2"),sQuery(id+"F2.wireOp",EDGE,"E17"),sQuery(id+"F2.wireOp",EDGE,"E18")])]}),"instanceName":"11"});
            var Q107;
            Q107=makeQuery(id+"F4.opPattern","COPY",BODY,{"derivedFrom":makeQuery(id+"F3.opExtrude","SWEPT_BODY",BODY,{"disambiguationData":[OSD([sQuery(id+"F0.wireOp",EDGE,"E1"),sQuery(id+"F0.wireOp",EDGE,"E2"),sQuery(id+"F2.wireOp",EDGE,"E17"),sQuery(id+"F2.wireOp",EDGE,"E18")])]}),"instanceName":"135"});
            var Q108;
            Q108=makeQuery(id+"F4.opPattern","COPY",BODY,{"derivedFrom":makeQuery(id+"F3.opExtrude","SWEPT_BODY",BODY,{"disambiguationData":[OSD([sQuery(id+"F0.wireOp",EDGE,"E1"),sQuery(id+"F0.wireOp",EDGE,"E2"),sQuery(id+"F2.wireOp",EDGE,"E17"),sQuery(id+"F2.wireOp",EDGE,"E18")])]}),"instanceName":"150"});
            var Q109;
            Q109=makeQuery(id+"F4.opPattern","COPY",BODY,{"derivedFrom":makeQuery(id+"F3.opExtrude","SWEPT_BODY",BODY,{"disambiguationData":[OSD([sQuery(id+"F0.wireOp",EDGE,"E1"),sQuery(id+"F0.wireOp",EDGE,"E2"),sQuery(id+"F2.wireOp",EDGE,"E17"),sQuery(id+"F2.wireOp",EDGE,"E18")])]}),"instanceName":"166"});
            var Q110;
            Q110=makeQuery(id+"F4.opPattern","COPY",BODY,{"derivedFrom":makeQuery(id+"F3.opExtrude","SWEPT_BODY",BODY,{"disambiguationData":[OSD([sQuery(id+"F0.wireOp",EDGE,"E1"),sQuery(id+"F0.wireOp",EDGE,"E2"),sQuery(id+"F2.wireOp",EDGE,"E17"),sQuery(id+"F2.wireOp",EDGE,"E18")])]}),"instanceName":"162"});
            var Q111;
            Q111=makeQuery(id+"F4.opPattern","COPY",BODY,{"derivedFrom":makeQuery(id+"F3.opExtrude","SWEPT_BODY",BODY,{"disambiguationData":[OSD([sQuery(id+"F0.wireOp",EDGE,"E1"),sQuery(id+"F0.wireOp",EDGE,"E2"),sQuery(id+"F2.wireOp",EDGE,"E17"),sQuery(id+"F2.wireOp",EDGE,"E18")])]}),"instanceName":"85"});
            var Q112;
            Q112=makeQuery(id+"F4.opPattern","COPY",BODY,{"derivedFrom":makeQuery(id+"F3.opExtrude","SWEPT_BODY",BODY,{"disambiguationData":[OSD([sQuery(id+"F0.wireOp",EDGE,"E1"),sQuery(id+"F0.wireOp",EDGE,"E2"),sQuery(id+"F2.wireOp",EDGE,"E17"),sQuery(id+"F2.wireOp",EDGE,"E18")])]}),"instanceName":"151"});
            var Q113;
            Q113=makeQuery(id+"F4.opPattern","COPY",BODY,{"derivedFrom":makeQuery(id+"F3.opExtrude","SWEPT_BODY",BODY,{"disambiguationData":[OSD([sQuery(id+"F0.wireOp",EDGE,"E1"),sQuery(id+"F0.wireOp",EDGE,"E2"),sQuery(id+"F2.wireOp",EDGE,"E17"),sQuery(id+"F2.wireOp",EDGE,"E18")])]}),"instanceName":"136"});
            var Q114;
            Q114=makeQuery(id+"F4.opPattern","COPY",BODY,{"derivedFrom":makeQuery(id+"F3.opExtrude","SWEPT_BODY",BODY,{"disambiguationData":[OSD([sQuery(id+"F0.wireOp",EDGE,"E1"),sQuery(id+"F0.wireOp",EDGE,"E2"),sQuery(id+"F2.wireOp",EDGE,"E17"),sQuery(id+"F2.wireOp",EDGE,"E18")])]}),"instanceName":"19"});
            var Q115;
            Q115=makeQuery(id+"F4.opPattern","COPY",BODY,{"derivedFrom":makeQuery(id+"F3.opExtrude","SWEPT_BODY",BODY,{"disambiguationData":[OSD([sQuery(id+"F0.wireOp",EDGE,"E1"),sQuery(id+"F0.wireOp",EDGE,"E2"),sQuery(id+"F2.wireOp",EDGE,"E17"),sQuery(id+"F2.wireOp",EDGE,"E18")])]}),"instanceName":"42"});
            var Q116;
            Q116=makeQuery(id+"F4.opPattern","COPY",BODY,{"derivedFrom":makeQuery(id+"F3.opExtrude","SWEPT_BODY",BODY,{"disambiguationData":[OSD([sQuery(id+"F0.wireOp",EDGE,"E1"),sQuery(id+"F0.wireOp",EDGE,"E2"),sQuery(id+"F2.wireOp",EDGE,"E17"),sQuery(id+"F2.wireOp",EDGE,"E18")])]}),"instanceName":"60"});
            var Q117;
            Q117=makeQuery(id+"F4.opPattern","COPY",BODY,{"derivedFrom":makeQuery(id+"F3.opExtrude","SWEPT_BODY",BODY,{"disambiguationData":[OSD([sQuery(id+"F0.wireOp",EDGE,"E1"),sQuery(id+"F0.wireOp",EDGE,"E2"),sQuery(id+"F2.wireOp",EDGE,"E17"),sQuery(id+"F2.wireOp",EDGE,"E18")])]}),"instanceName":"112"});
            var Q118;
            Q118=makeQuery(id+"F4.opPattern","COPY",BODY,{"derivedFrom":makeQuery(id+"F3.opExtrude","SWEPT_BODY",BODY,{"disambiguationData":[OSD([sQuery(id+"F0.wireOp",EDGE,"E1"),sQuery(id+"F0.wireOp",EDGE,"E2"),sQuery(id+"F2.wireOp",EDGE,"E17"),sQuery(id+"F2.wireOp",EDGE,"E18")])]}),"instanceName":"30"});
            var Q119;
            Q119=makeQuery(id+"F4.opPattern","COPY",BODY,{"derivedFrom":makeQuery(id+"F3.opExtrude","SWEPT_BODY",BODY,{"disambiguationData":[OSD([sQuery(id+"F0.wireOp",EDGE,"E1"),sQuery(id+"F0.wireOp",EDGE,"E2"),sQuery(id+"F2.wireOp",EDGE,"E17"),sQuery(id+"F2.wireOp",EDGE,"E18")])]}),"instanceName":"73"});
            var Q120;
            Q120=makeQuery(id+"F4.opPattern","COPY",BODY,{"derivedFrom":makeQuery(id+"F3.opExtrude","SWEPT_BODY",BODY,{"disambiguationData":[OSD([sQuery(id+"F0.wireOp",EDGE,"E1"),sQuery(id+"F0.wireOp",EDGE,"E2"),sQuery(id+"F2.wireOp",EDGE,"E17"),sQuery(id+"F2.wireOp",EDGE,"E18")])]}),"instanceName":"58"});
            var Q121;
            Q121=makeQuery(id+"F4.opPattern","COPY",BODY,{"derivedFrom":makeQuery(id+"F3.opExtrude","SWEPT_BODY",BODY,{"disambiguationData":[OSD([sQuery(id+"F0.wireOp",EDGE,"E1"),sQuery(id+"F0.wireOp",EDGE,"E2"),sQuery(id+"F2.wireOp",EDGE,"E17"),sQuery(id+"F2.wireOp",EDGE,"E18")])]}),"instanceName":"99"});
            var Q122;
            Q122=makeQuery(id+"F4.opPattern","COPY",BODY,{"derivedFrom":makeQuery(id+"F3.opExtrude","SWEPT_BODY",BODY,{"disambiguationData":[OSD([sQuery(id+"F0.wireOp",EDGE,"E1"),sQuery(id+"F0.wireOp",EDGE,"E2"),sQuery(id+"F2.wireOp",EDGE,"E17"),sQuery(id+"F2.wireOp",EDGE,"E18")])]}),"instanceName":"172"});
            var Q123;
            Q123=makeQuery(id+"F4.opPattern","COPY",BODY,{"derivedFrom":makeQuery(id+"F3.opExtrude","SWEPT_BODY",BODY,{"disambiguationData":[OSD([sQuery(id+"F0.wireOp",EDGE,"E1"),sQuery(id+"F0.wireOp",EDGE,"E2"),sQuery(id+"F2.wireOp",EDGE,"E17"),sQuery(id+"F2.wireOp",EDGE,"E18")])]}),"instanceName":"86"});
            var Q124;
            Q124=makeQuery(id+"F4.opPattern","COPY",BODY,{"derivedFrom":makeQuery(id+"F3.opExtrude","SWEPT_BODY",BODY,{"disambiguationData":[OSD([sQuery(id+"F0.wireOp",EDGE,"E1"),sQuery(id+"F0.wireOp",EDGE,"E2"),sQuery(id+"F2.wireOp",EDGE,"E17"),sQuery(id+"F2.wireOp",EDGE,"E18")])]}),"instanceName":"56"});
            var Q125;
            Q125=makeQuery(id+"F4.opPattern","COPY",BODY,{"derivedFrom":makeQuery(id+"F3.opExtrude","SWEPT_BODY",BODY,{"disambiguationData":[OSD([sQuery(id+"F0.wireOp",EDGE,"E1"),sQuery(id+"F0.wireOp",EDGE,"E2"),sQuery(id+"F2.wireOp",EDGE,"E17"),sQuery(id+"F2.wireOp",EDGE,"E18")])]}),"instanceName":"94"});
            var Q126;
            Q126=makeQuery(id+"F4.opPattern","COPY",BODY,{"derivedFrom":makeQuery(id+"F3.opExtrude","SWEPT_BODY",BODY,{"disambiguationData":[OSD([sQuery(id+"F0.wireOp",EDGE,"E1"),sQuery(id+"F0.wireOp",EDGE,"E2"),sQuery(id+"F2.wireOp",EDGE,"E17"),sQuery(id+"F2.wireOp",EDGE,"E18")])]}),"instanceName":"87"});
            var Q127;
            Q127=makeQuery(id+"F4.opPattern","COPY",BODY,{"derivedFrom":makeQuery(id+"F3.opExtrude","SWEPT_BODY",BODY,{"disambiguationData":[OSD([sQuery(id+"F0.wireOp",EDGE,"E1"),sQuery(id+"F0.wireOp",EDGE,"E2"),sQuery(id+"F2.wireOp",EDGE,"E17"),sQuery(id+"F2.wireOp",EDGE,"E18")])]}),"instanceName":"143"});
            var Q128;
            Q128=makeQuery(id+"F4.opPattern","COPY",BODY,{"derivedFrom":makeQuery(id+"F3.opExtrude","SWEPT_BODY",BODY,{"disambiguationData":[OSD([sQuery(id+"F0.wireOp",EDGE,"E1"),sQuery(id+"F0.wireOp",EDGE,"E2"),sQuery(id+"F2.wireOp",EDGE,"E17"),sQuery(id+"F2.wireOp",EDGE,"E18")])]}),"instanceName":"49"});
            var Q129;
            Q129=makeQuery(id+"F4.opPattern","COPY",BODY,{"derivedFrom":makeQuery(id+"F3.opExtrude","SWEPT_BODY",BODY,{"disambiguationData":[OSD([sQuery(id+"F0.wireOp",EDGE,"E1"),sQuery(id+"F0.wireOp",EDGE,"E2"),sQuery(id+"F2.wireOp",EDGE,"E17"),sQuery(id+"F2.wireOp",EDGE,"E18")])]}),"instanceName":"167"});
            var Q130;
            Q130=makeQuery(id+"F4.opPattern","COPY",BODY,{"derivedFrom":makeQuery(id+"F3.opExtrude","SWEPT_BODY",BODY,{"disambiguationData":[OSD([sQuery(id+"F0.wireOp",EDGE,"E1"),sQuery(id+"F0.wireOp",EDGE,"E2"),sQuery(id+"F2.wireOp",EDGE,"E17"),sQuery(id+"F2.wireOp",EDGE,"E18")])]}),"instanceName":"72"});
            var Q131;
            Q131=makeQuery(id+"F4.opPattern","COPY",BODY,{"derivedFrom":makeQuery(id+"F3.opExtrude","SWEPT_BODY",BODY,{"disambiguationData":[OSD([sQuery(id+"F0.wireOp",EDGE,"E1"),sQuery(id+"F0.wireOp",EDGE,"E2"),sQuery(id+"F2.wireOp",EDGE,"E17"),sQuery(id+"F2.wireOp",EDGE,"E18")])]}),"instanceName":"133"});
            var Q132;
            Q132=makeQuery(id+"F4.opPattern","COPY",BODY,{"derivedFrom":makeQuery(id+"F3.opExtrude","SWEPT_BODY",BODY,{"disambiguationData":[OSD([sQuery(id+"F0.wireOp",EDGE,"E1"),sQuery(id+"F0.wireOp",EDGE,"E2"),sQuery(id+"F2.wireOp",EDGE,"E17"),sQuery(id+"F2.wireOp",EDGE,"E18")])]}),"instanceName":"123"});
            var Q133;
            Q133=makeQuery(id+"F4.opPattern","COPY",BODY,{"derivedFrom":makeQuery(id+"F3.opExtrude","SWEPT_BODY",BODY,{"disambiguationData":[OSD([sQuery(id+"F0.wireOp",EDGE,"E1"),sQuery(id+"F0.wireOp",EDGE,"E2"),sQuery(id+"F2.wireOp",EDGE,"E17"),sQuery(id+"F2.wireOp",EDGE,"E18")])]}),"instanceName":"12"});
            var Q134;
            Q134=makeQuery(id+"F4.opPattern","COPY",BODY,{"derivedFrom":makeQuery(id+"F3.opExtrude","SWEPT_BODY",BODY,{"disambiguationData":[OSD([sQuery(id+"F0.wireOp",EDGE,"E1"),sQuery(id+"F0.wireOp",EDGE,"E2"),sQuery(id+"F2.wireOp",EDGE,"E17"),sQuery(id+"F2.wireOp",EDGE,"E18")])]}),"instanceName":"6"});
            var Q135;
            Q135=makeQuery(id+"F4.opPattern","COPY",BODY,{"derivedFrom":makeQuery(id+"F3.opExtrude","SWEPT_BODY",BODY,{"disambiguationData":[OSD([sQuery(id+"F0.wireOp",EDGE,"E1"),sQuery(id+"F0.wireOp",EDGE,"E2"),sQuery(id+"F2.wireOp",EDGE,"E17"),sQuery(id+"F2.wireOp",EDGE,"E18")])]}),"instanceName":"59"});
            var Q136;
            Q136=makeQuery(id+"F4.opPattern","COPY",BODY,{"derivedFrom":makeQuery(id+"F3.opExtrude","SWEPT_BODY",BODY,{"disambiguationData":[OSD([sQuery(id+"F0.wireOp",EDGE,"E1"),sQuery(id+"F0.wireOp",EDGE,"E2"),sQuery(id+"F2.wireOp",EDGE,"E17"),sQuery(id+"F2.wireOp",EDGE,"E18")])]}),"instanceName":"17"});
            var Q137;
            Q137=makeQuery(id+"F4.opPattern","COPY",BODY,{"derivedFrom":makeQuery(id+"F3.opExtrude","SWEPT_BODY",BODY,{"disambiguationData":[OSD([sQuery(id+"F0.wireOp",EDGE,"E1"),sQuery(id+"F0.wireOp",EDGE,"E2"),sQuery(id+"F2.wireOp",EDGE,"E17"),sQuery(id+"F2.wireOp",EDGE,"E18")])]}),"instanceName":"63"});
            var Q138;
            Q138=makeQuery(id+"F4.opPattern","COPY",BODY,{"derivedFrom":makeQuery(id+"F3.opExtrude","SWEPT_BODY",BODY,{"disambiguationData":[OSD([sQuery(id+"F0.wireOp",EDGE,"E1"),sQuery(id+"F0.wireOp",EDGE,"E2"),sQuery(id+"F2.wireOp",EDGE,"E17"),sQuery(id+"F2.wireOp",EDGE,"E18")])]}),"instanceName":"163"});
            var Q139;
            Q139=makeQuery(id+"F4.opPattern","COPY",BODY,{"derivedFrom":makeQuery(id+"F3.opExtrude","SWEPT_BODY",BODY,{"disambiguationData":[OSD([sQuery(id+"F0.wireOp",EDGE,"E1"),sQuery(id+"F0.wireOp",EDGE,"E2"),sQuery(id+"F2.wireOp",EDGE,"E17"),sQuery(id+"F2.wireOp",EDGE,"E18")])]}),"instanceName":"2"});
            var Q140;
            Q140=makeQuery(id+"F4.opPattern","COPY",BODY,{"derivedFrom":makeQuery(id+"F3.opExtrude","SWEPT_BODY",BODY,{"disambiguationData":[OSD([sQuery(id+"F0.wireOp",EDGE,"E1"),sQuery(id+"F0.wireOp",EDGE,"E2"),sQuery(id+"F2.wireOp",EDGE,"E17"),sQuery(id+"F2.wireOp",EDGE,"E18")])]}),"instanceName":"68"});
            var Q141;
            Q141=makeQuery(id+"F4.opPattern","COPY",BODY,{"derivedFrom":makeQuery(id+"F3.opExtrude","SWEPT_BODY",BODY,{"disambiguationData":[OSD([sQuery(id+"F0.wireOp",EDGE,"E1"),sQuery(id+"F0.wireOp",EDGE,"E2"),sQuery(id+"F2.wireOp",EDGE,"E17"),sQuery(id+"F2.wireOp",EDGE,"E18")])]}),"instanceName":"129"});
            var Q142;
            Q142=makeQuery(id+"F4.opPattern","COPY",BODY,{"derivedFrom":makeQuery(id+"F3.opExtrude","SWEPT_BODY",BODY,{"disambiguationData":[OSD([sQuery(id+"F0.wireOp",EDGE,"E1"),sQuery(id+"F0.wireOp",EDGE,"E2"),sQuery(id+"F2.wireOp",EDGE,"E17"),sQuery(id+"F2.wireOp",EDGE,"E18")])]}),"instanceName":"70"});
            var Q143;
            Q143=makeQuery(id+"F4.opPattern","COPY",BODY,{"derivedFrom":makeQuery(id+"F3.opExtrude","SWEPT_BODY",BODY,{"disambiguationData":[OSD([sQuery(id+"F0.wireOp",EDGE,"E1"),sQuery(id+"F0.wireOp",EDGE,"E2"),sQuery(id+"F2.wireOp",EDGE,"E17"),sQuery(id+"F2.wireOp",EDGE,"E18")])]}),"instanceName":"111"});
            var Q144;
            Q144=makeQuery(id+"F4.opPattern","COPY",BODY,{"derivedFrom":makeQuery(id+"F3.opExtrude","SWEPT_BODY",BODY,{"disambiguationData":[OSD([sQuery(id+"F0.wireOp",EDGE,"E1"),sQuery(id+"F0.wireOp",EDGE,"E2"),sQuery(id+"F2.wireOp",EDGE,"E17"),sQuery(id+"F2.wireOp",EDGE,"E18")])]}),"instanceName":"16"});
            var Q145;
            Q145=makeQuery(id+"F4.opPattern","COPY",BODY,{"derivedFrom":makeQuery(id+"F3.opExtrude","SWEPT_BODY",BODY,{"disambiguationData":[OSD([sQuery(id+"F0.wireOp",EDGE,"E1"),sQuery(id+"F0.wireOp",EDGE,"E2"),sQuery(id+"F2.wireOp",EDGE,"E17"),sQuery(id+"F2.wireOp",EDGE,"E18")])]}),"instanceName":"144"});
            var Q146;
            Q146=makeQuery(id+"F4.opPattern","COPY",BODY,{"derivedFrom":makeQuery(id+"F3.opExtrude","SWEPT_BODY",BODY,{"disambiguationData":[OSD([sQuery(id+"F0.wireOp",EDGE,"E1"),sQuery(id+"F0.wireOp",EDGE,"E2"),sQuery(id+"F2.wireOp",EDGE,"E17"),sQuery(id+"F2.wireOp",EDGE,"E18")])]}),"instanceName":"139"});
            var Q147;
            Q147=makeQuery(id+"F4.opPattern","COPY",BODY,{"derivedFrom":makeQuery(id+"F3.opExtrude","SWEPT_BODY",BODY,{"disambiguationData":[OSD([sQuery(id+"F0.wireOp",EDGE,"E1"),sQuery(id+"F0.wireOp",EDGE,"E2"),sQuery(id+"F2.wireOp",EDGE,"E17"),sQuery(id+"F2.wireOp",EDGE,"E18")])]}),"instanceName":"38"});
            var Q148;
            Q148=makeQuery(id+"F4.opPattern","COPY",BODY,{"derivedFrom":makeQuery(id+"F3.opExtrude","SWEPT_BODY",BODY,{"disambiguationData":[OSD([sQuery(id+"F0.wireOp",EDGE,"E1"),sQuery(id+"F0.wireOp",EDGE,"E2"),sQuery(id+"F2.wireOp",EDGE,"E17"),sQuery(id+"F2.wireOp",EDGE,"E18")])]}),"instanceName":"120"});
            var Q149;
            Q149=makeQuery(id+"F4.opPattern","COPY",BODY,{"derivedFrom":makeQuery(id+"F3.opExtrude","SWEPT_BODY",BODY,{"disambiguationData":[OSD([sQuery(id+"F0.wireOp",EDGE,"E1"),sQuery(id+"F0.wireOp",EDGE,"E2"),sQuery(id+"F2.wireOp",EDGE,"E17"),sQuery(id+"F2.wireOp",EDGE,"E18")])]}),"instanceName":"32"});
            var Q150;
            Q150=makeQuery(id+"F4.opPattern","COPY",BODY,{"derivedFrom":makeQuery(id+"F3.opExtrude","SWEPT_BODY",BODY,{"disambiguationData":[OSD([sQuery(id+"F0.wireOp",EDGE,"E1"),sQuery(id+"F0.wireOp",EDGE,"E2"),sQuery(id+"F2.wireOp",EDGE,"E17"),sQuery(id+"F2.wireOp",EDGE,"E18")])]}),"instanceName":"105"});
            var Q151;
            Q151=makeQuery(id+"F4.opPattern","COPY",BODY,{"derivedFrom":makeQuery(id+"F3.opExtrude","SWEPT_BODY",BODY,{"disambiguationData":[OSD([sQuery(id+"F0.wireOp",EDGE,"E1"),sQuery(id+"F0.wireOp",EDGE,"E2"),sQuery(id+"F2.wireOp",EDGE,"E17"),sQuery(id+"F2.wireOp",EDGE,"E18")])]}),"instanceName":"35"});
            var Q152;
            Q152=makeQuery(id+"F4.opPattern","COPY",BODY,{"derivedFrom":makeQuery(id+"F3.opExtrude","SWEPT_BODY",BODY,{"disambiguationData":[OSD([sQuery(id+"F0.wireOp",EDGE,"E1"),sQuery(id+"F0.wireOp",EDGE,"E2"),sQuery(id+"F2.wireOp",EDGE,"E17"),sQuery(id+"F2.wireOp",EDGE,"E18")])]}),"instanceName":"132"});
            var Q153;
            Q153=makeQuery(id+"F4.opPattern","COPY",BODY,{"derivedFrom":makeQuery(id+"F3.opExtrude","SWEPT_BODY",BODY,{"disambiguationData":[OSD([sQuery(id+"F0.wireOp",EDGE,"E1"),sQuery(id+"F0.wireOp",EDGE,"E2"),sQuery(id+"F2.wireOp",EDGE,"E17"),sQuery(id+"F2.wireOp",EDGE,"E18")])]}),"instanceName":"69"});
            var Q154;
            Q154=makeQuery(id+"F4.opPattern","COPY",BODY,{"derivedFrom":makeQuery(id+"F3.opExtrude","SWEPT_BODY",BODY,{"disambiguationData":[OSD([sQuery(id+"F0.wireOp",EDGE,"E1"),sQuery(id+"F0.wireOp",EDGE,"E2"),sQuery(id+"F2.wireOp",EDGE,"E17"),sQuery(id+"F2.wireOp",EDGE,"E18")])]}),"instanceName":"79"});
            var Q155;
            Q155=makeQuery(id+"F4.opPattern","COPY",BODY,{"derivedFrom":makeQuery(id+"F3.opExtrude","SWEPT_BODY",BODY,{"disambiguationData":[OSD([sQuery(id+"F0.wireOp",EDGE,"E1"),sQuery(id+"F0.wireOp",EDGE,"E2"),sQuery(id+"F2.wireOp",EDGE,"E17"),sQuery(id+"F2.wireOp",EDGE,"E18")])]}),"instanceName":"131"});
            var Q156;
            Q156=makeQuery(id+"F4.opPattern","COPY",BODY,{"derivedFrom":makeQuery(id+"F3.opExtrude","SWEPT_BODY",BODY,{"disambiguationData":[OSD([sQuery(id+"F0.wireOp",EDGE,"E1"),sQuery(id+"F0.wireOp",EDGE,"E2"),sQuery(id+"F2.wireOp",EDGE,"E17"),sQuery(id+"F2.wireOp",EDGE,"E18")])]}),"instanceName":"26"});
            var Q157;
            Q157=makeQuery(id+"F4.opPattern","COPY",BODY,{"derivedFrom":makeQuery(id+"F3.opExtrude","SWEPT_BODY",BODY,{"disambiguationData":[OSD([sQuery(id+"F0.wireOp",EDGE,"E1"),sQuery(id+"F0.wireOp",EDGE,"E2"),sQuery(id+"F2.wireOp",EDGE,"E17"),sQuery(id+"F2.wireOp",EDGE,"E18")])]}),"instanceName":"158"});
            var Q158;
            Q158=makeQuery(id+"F4.opPattern","COPY",BODY,{"derivedFrom":makeQuery(id+"F3.opExtrude","SWEPT_BODY",BODY,{"disambiguationData":[OSD([sQuery(id+"F0.wireOp",EDGE,"E1"),sQuery(id+"F0.wireOp",EDGE,"E2"),sQuery(id+"F2.wireOp",EDGE,"E17"),sQuery(id+"F2.wireOp",EDGE,"E18")])]}),"instanceName":"91"});
            var Q159;
            Q159=makeQuery(id+"F4.opPattern","COPY",BODY,{"derivedFrom":makeQuery(id+"F3.opExtrude","SWEPT_BODY",BODY,{"disambiguationData":[OSD([sQuery(id+"F0.wireOp",EDGE,"E1"),sQuery(id+"F0.wireOp",EDGE,"E2"),sQuery(id+"F2.wireOp",EDGE,"E17"),sQuery(id+"F2.wireOp",EDGE,"E18")])]}),"instanceName":"118"});
            var Q160;
            Q160=makeQuery(id+"F4.opPattern","COPY",BODY,{"derivedFrom":makeQuery(id+"F3.opExtrude","SWEPT_BODY",BODY,{"disambiguationData":[OSD([sQuery(id+"F0.wireOp",EDGE,"E1"),sQuery(id+"F0.wireOp",EDGE,"E2"),sQuery(id+"F2.wireOp",EDGE,"E17"),sQuery(id+"F2.wireOp",EDGE,"E18")])]}),"instanceName":"90"});
            var Q161;
            Q161=makeQuery(id+"F4.opPattern","COPY",BODY,{"derivedFrom":makeQuery(id+"F3.opExtrude","SWEPT_BODY",BODY,{"disambiguationData":[OSD([sQuery(id+"F0.wireOp",EDGE,"E1"),sQuery(id+"F0.wireOp",EDGE,"E2"),sQuery(id+"F2.wireOp",EDGE,"E17"),sQuery(id+"F2.wireOp",EDGE,"E18")])]}),"instanceName":"8"});
            var Q162;
            Q162=makeQuery(id+"F4.opPattern","COPY",BODY,{"derivedFrom":makeQuery(id+"F3.opExtrude","SWEPT_BODY",BODY,{"disambiguationData":[OSD([sQuery(id+"F0.wireOp",EDGE,"E1"),sQuery(id+"F0.wireOp",EDGE,"E2"),sQuery(id+"F2.wireOp",EDGE,"E17"),sQuery(id+"F2.wireOp",EDGE,"E18")])]}),"instanceName":"76"});
            var Q163;
            Q163=makeQuery(id+"F4.opPattern","COPY",BODY,{"derivedFrom":makeQuery(id+"F3.opExtrude","SWEPT_BODY",BODY,{"disambiguationData":[OSD([sQuery(id+"F0.wireOp",EDGE,"E1"),sQuery(id+"F0.wireOp",EDGE,"E2"),sQuery(id+"F2.wireOp",EDGE,"E17"),sQuery(id+"F2.wireOp",EDGE,"E18")])]}),"instanceName":"54"});
            var Q164;
            Q164=makeQuery(id+"F4.opPattern","COPY",BODY,{"derivedFrom":makeQuery(id+"F3.opExtrude","SWEPT_BODY",BODY,{"disambiguationData":[OSD([sQuery(id+"F0.wireOp",EDGE,"E1"),sQuery(id+"F0.wireOp",EDGE,"E2"),sQuery(id+"F2.wireOp",EDGE,"E17"),sQuery(id+"F2.wireOp",EDGE,"E18")])]}),"instanceName":"97"});
            var Q165;
            Q165=makeQuery(id+"F4.opPattern","COPY",BODY,{"derivedFrom":makeQuery(id+"F3.opExtrude","SWEPT_BODY",BODY,{"disambiguationData":[OSD([sQuery(id+"F0.wireOp",EDGE,"E1"),sQuery(id+"F0.wireOp",EDGE,"E2"),sQuery(id+"F2.wireOp",EDGE,"E17"),sQuery(id+"F2.wireOp",EDGE,"E18")])]}),"instanceName":"5"});
            var Q166;
            Q166=makeQuery(id+"F4.opPattern","COPY",BODY,{"derivedFrom":makeQuery(id+"F3.opExtrude","SWEPT_BODY",BODY,{"disambiguationData":[OSD([sQuery(id+"F0.wireOp",EDGE,"E1"),sQuery(id+"F0.wireOp",EDGE,"E2"),sQuery(id+"F2.wireOp",EDGE,"E17"),sQuery(id+"F2.wireOp",EDGE,"E18")])]}),"instanceName":"161"});
            var Q167;
            Q167=makeQuery(id+"F4.opPattern","COPY",BODY,{"derivedFrom":makeQuery(id+"F3.opExtrude","SWEPT_BODY",BODY,{"disambiguationData":[OSD([sQuery(id+"F0.wireOp",EDGE,"E1"),sQuery(id+"F0.wireOp",EDGE,"E2"),sQuery(id+"F2.wireOp",EDGE,"E17"),sQuery(id+"F2.wireOp",EDGE,"E18")])]}),"instanceName":"46"});
            var Q168;
            Q168=makeQuery(id+"F4.opPattern","COPY",BODY,{"derivedFrom":makeQuery(id+"F3.opExtrude","SWEPT_BODY",BODY,{"disambiguationData":[OSD([sQuery(id+"F0.wireOp",EDGE,"E1"),sQuery(id+"F0.wireOp",EDGE,"E2"),sQuery(id+"F2.wireOp",EDGE,"E17"),sQuery(id+"F2.wireOp",EDGE,"E18")])]}),"instanceName":"71"});
            var Q169;
            Q169=makeQuery(id+"F4.opPattern","COPY",BODY,{"derivedFrom":makeQuery(id+"F3.opExtrude","SWEPT_BODY",BODY,{"disambiguationData":[OSD([sQuery(id+"F0.wireOp",EDGE,"E1"),sQuery(id+"F0.wireOp",EDGE,"E2"),sQuery(id+"F2.wireOp",EDGE,"E17"),sQuery(id+"F2.wireOp",EDGE,"E18")])]}),"instanceName":"80"});
            var Q170;
            Q170=makeQuery(id+"F4.opPattern","COPY",BODY,{"derivedFrom":makeQuery(id+"F3.opExtrude","SWEPT_BODY",BODY,{"disambiguationData":[OSD([sQuery(id+"F0.wireOp",EDGE,"E1"),sQuery(id+"F0.wireOp",EDGE,"E2"),sQuery(id+"F2.wireOp",EDGE,"E17"),sQuery(id+"F2.wireOp",EDGE,"E18")])]}),"instanceName":"25"});
            var Q171;
            Q171=makeQuery(id+"F4.opPattern","COPY",BODY,{"derivedFrom":makeQuery(id+"F3.opExtrude","SWEPT_BODY",BODY,{"disambiguationData":[OSD([sQuery(id+"F0.wireOp",EDGE,"E1"),sQuery(id+"F0.wireOp",EDGE,"E2"),sQuery(id+"F2.wireOp",EDGE,"E17"),sQuery(id+"F2.wireOp",EDGE,"E18")])]}),"instanceName":"155"});
            var Q172;
            Q172=makeQuery(id+"F4.opPattern","COPY",BODY,{"derivedFrom":makeQuery(id+"F3.opExtrude","SWEPT_BODY",BODY,{"disambiguationData":[OSD([sQuery(id+"F0.wireOp",EDGE,"E1"),sQuery(id+"F0.wireOp",EDGE,"E2"),sQuery(id+"F2.wireOp",EDGE,"E17"),sQuery(id+"F2.wireOp",EDGE,"E18")])]}),"instanceName":"89"});
            var Q173;
            Q173=makeQuery(id+"F1.opRevolve","SWEPT_BODY",BODY,{"disambiguationData":[OSD([sQuery(id+"F0.wireOp",EDGE,"E0"),sQuery(id+"F0.wireOp",EDGE,"E1"),sQuery(id+"F0.wireOp",EDGE,"E2"),sQuery(id+"F0.wireOp",EDGE,"E3"),sQuery(id+"F0.wireOp",EDGE,"E4"),sQuery(id+"F0.wireOp",EDGE,"E5"),sQuery(id+"F0.wireOp",EDGE,"E6"),sQuery(id+"F0.wireOp",EDGE,"E7"),sQuery(id+"F0.wireOp",EDGE,"E8"),sQuery(id+"F0.wireOp",EDGE,"E9"),sQuery(id+"F0.wireOp",EDGE,"E10"),sQuery(id+"F0.wireOp",EDGE,"E11"),sQuery(id+"F0.wireOp",EDGE,"E12"),sQuery(id+"F0.wireOp",EDGE,"E13"),sQuery(id+"F0.wireOp",EDGE,"E14")])]});
            booleanBodies(context, id + "F5", {"operationType" : BooleanOperationType.SUBTRACTION, "tools" : qUnion([Q0, Q1, Q2, Q3, Q4, Q5, Q6, Q7, Q8, Q9, Q10, Q11, Q12, Q13, Q14, Q15, Q16, Q17, Q18, Q19, Q20, Q21, Q22, Q23, Q24, Q25, Q26, Q27, Q28, Q29, Q30, Q31, Q32, Q33, Q34, Q35, Q36, Q37, Q38, Q39, Q40, Q41, Q42, Q43, Q44, Q45, Q46, Q47, Q48, Q49, Q50, Q51, Q52, Q53, Q54, Q55, Q56, Q57, Q58, Q59, Q60, Q61, Q62, Q63, Q64, Q65, Q66, Q67, Q68, Q69, Q70, Q71, Q72, Q73, Q74, Q75, Q76, Q77, Q78, Q79, Q80, Q81, Q82, Q83, Q84, Q85, Q86, Q87, Q88, Q89, Q90, Q91, Q92, Q93, Q94, Q95, Q96, Q97, Q98, Q99, Q100, Q101, Q102, Q103, Q104, Q105, Q106, Q107, Q108, Q109, Q110, Q111, Q112, Q113, Q114, Q115, Q116, Q117, Q118, Q119, Q120, Q121, Q122, Q123, Q124, Q125, Q126, Q127, Q128, Q129, Q130, Q131, Q132, Q133, Q134, Q135, Q136, Q137, Q138, Q139, Q140, Q141, Q142, Q143, Q144, Q145, Q146, Q147, Q148, Q149, Q150, Q151, Q152, Q153, Q154, Q155, Q156, Q157, Q158, Q159, Q160, Q161, Q162, Q163, Q164, Q165, Q166, Q167, Q168, Q169, Q170, Q171, Q172]), "targets" : qUnion([Q173])});
        }
        {
            var Q0;
            Q0=makeQuery(id+"F1.opRevolve","SWEPT_FACE",FACE,{"disambiguationData":[OSD([sQuery(id+"F0.wireOp",EDGE,"E7")])]});
            cPlane(context, id + "F6", {"entities" : qUnion([Q0]), "cplaneType" : CPlaneType.OFFSET, "offset" : 3.2 * mm, "oppositeDirection" : true, "width" : 150 * mm, "height" : 150 * mm});
        }
        {
            var Q0;
            Q0=qCreatedBy(id+"F6.planeOp",FACE);
            var sketch = newSketch(context, id + "F7", { "sketchPlane" : qUnion([Q0])});
            skCircle(sketch, "E20", {"center": v(0, 0) * mm, "radius": 5 * mm});
            skLineSegment(sketch, "E21", {"start": v(-3.92, -3.1) * mm, "end": v(3.92, -3.1) * mm});
            skLineSegment(sketch, "E22", {"start": v(3.92, 3.1) * mm, "end": v(-3.92, 3.1) * mm});
            skSolve(sketch);
        }
        {
            var Q0;
            {var subQ0=sQuery(id+"F7.wireOp",EDGE,"E21");Q0=makeQuery(id+"F7.imprint","IMPRINT",FACE,{"disambiguationData":[TD([[makeQuery(id+"F7.imprint","IMPRINT",EDGE,{"derivedFrom":subQ0}),-1.0]])]});}
            var Q1;
            {var subQ0=sQuery(id+"F7.wireOp",EDGE,"E22");Q1=makeQuery(id+"F7.imprint","IMPRINT",FACE,{"disambiguationData":[TD([[makeQuery(id+"F7.imprint","IMPRINT",EDGE,{"derivedFrom":subQ0}),-1.0]])]});}
            extrude(context, id + "F8", {"entities" : qUnion([Q0, Q1]), "operationType" : NewBodyOperationType.REMOVE, "oppositeDirection" : true, "depth" : 0.8 * mm});
        }
        {
            var Q0;
            Q0=makeQuery(id+"F1.opRevolve","SWEPT_FACE",FACE,{"disambiguationData":[OSD([sQuery(id+"F0.wireOp",EDGE,"E7")])]});
            var sketch = newSketch(context, id + "F9", { "sketchPlane" : qUnion([Q0])});
            skCircle(sketch, "E23", {"center": v(0, -12.25) * mm, "radius": 1.75 * mm});
            skLineSegment(sketch, "E24", {"start": v(-0.45, -10.56) * mm, "end": v(-6.76, -12.25) * mm});
            skLineSegment(sketch, "E25", {"start": v(-6.76, -12.25) * mm, "end": v(0, -12.25) * mm, "construction": true});
            skSolve(sketch);
        }
        {
            var Q0;
            {var subQ1=sQuery(id+"F9.wireOp",EDGE,"E23");var subQ4=makeQuery(id+"F9.imprint","INTERSECT",VERTEX,{"derivedFrom":[subQ1,sQuery(id+"F9.wireOp",EDGE,"E24")]});Q0=makeQuery(id+"F9.imprint","IMPRINT",FACE,{"disambiguationData":[TD([[makeQuery(id+"F9.imprint","IMPRINT",EDGE,{"disambiguationData":[TD([[subQ4,1.0]])],"derivedFrom":subQ1}),1.0]])]});}
            var Q1;
            Q1=makeQuery(id+"F1.opRevolve","SWEPT_FACE",FACE,{"disambiguationData":[OSD([sQuery(id+"F0.wireOp",EDGE,"E5")])]});
            extrude(context, id + "F10", {"entities" : qUnion([Q0]), "operationType" : NewBodyOperationType.REMOVE, "endBound" : BoundingType.UP_TO_SURFACE, "oppositeDirection" : true, "endBoundEntityFace" : qUnion([Q1]), "depth" : 25 * mm});
        }
        {
            var Q0;
            Q0=makeQuery(id+"F1.opRevolve","SWEPT_FACE",FACE,{"disambiguationData":[OSD([sQuery(id+"F0.wireOp",EDGE,"E9")])]});
            var sketch = newSketch(context, id + "F11", { "sketchPlane" : qUnion([Q0])});
            skLineSegment(sketch, "E26", {"start": v(-0.55, 4.97) * mm, "end": v(-0.55, -4.97) * mm});
            skLineSegment(sketch, "E27", {"start": v(0.55, -4.97) * mm, "end": v(0.55, 4.97) * mm});
            skSolve(sketch);
        }
        {
            var Q0;
            {var subQ0=sQuery(id+"F0.wireOp",EDGE,"E9");var subQ4=sQuery(id+"F11.wireOp",EDGE,"E26");var subQ6=makeQuery(id+"F1.opRevolve","SWEPT_EDGE",EDGE,{"disambiguationData":[OSD([sQuery(id+"F0.wireOp",EDGE,"E8"),subQ0])]});var subQ8=makeQuery(id+"F11.imprint","INTERSECT",VERTEX,{"disambiguationData":[OD(0.0)],"derivedFrom":[subQ6,subQ4]});Q0=makeQuery(id+"F11.imprint","IMPRINT",FACE,{"disambiguationData":[TD([[makeQuery(id+"F11.imprint","IMPRINT",EDGE,{"disambiguationData":[TD([[subQ8,-1.0]])],"derivedFrom":subQ4}),1.0]])]});}
            var Q1;
            {var subQ0=sQuery(id+"F0.wireOp",EDGE,"E9");var subQ4=sQuery(id+"F11.wireOp",EDGE,"E26");var subQ6=makeQuery(id+"F1.opRevolve","SWEPT_EDGE",EDGE,{"disambiguationData":[OSD([sQuery(id+"F0.wireOp",EDGE,"E8"),subQ0])]});var subQ8=makeQuery(id+"F11.imprint","INTERSECT",VERTEX,{"disambiguationData":[OD(1.0)],"derivedFrom":[subQ6,subQ4]});Q1=makeQuery(id+"F11.imprint","IMPRINT",FACE,{"disambiguationData":[TD([[makeQuery(id+"F11.imprint","IMPRINT",EDGE,{"disambiguationData":[TD([[subQ8,1.0]])],"derivedFrom":subQ4}),1.0]])]});}
            extrude(context, id + "F12", {"entities" : qUnion([Q0, Q1]), "operationType" : NewBodyOperationType.REMOVE, "oppositeDirection" : true, "depth" : 4.9 * mm});
        }
    });
